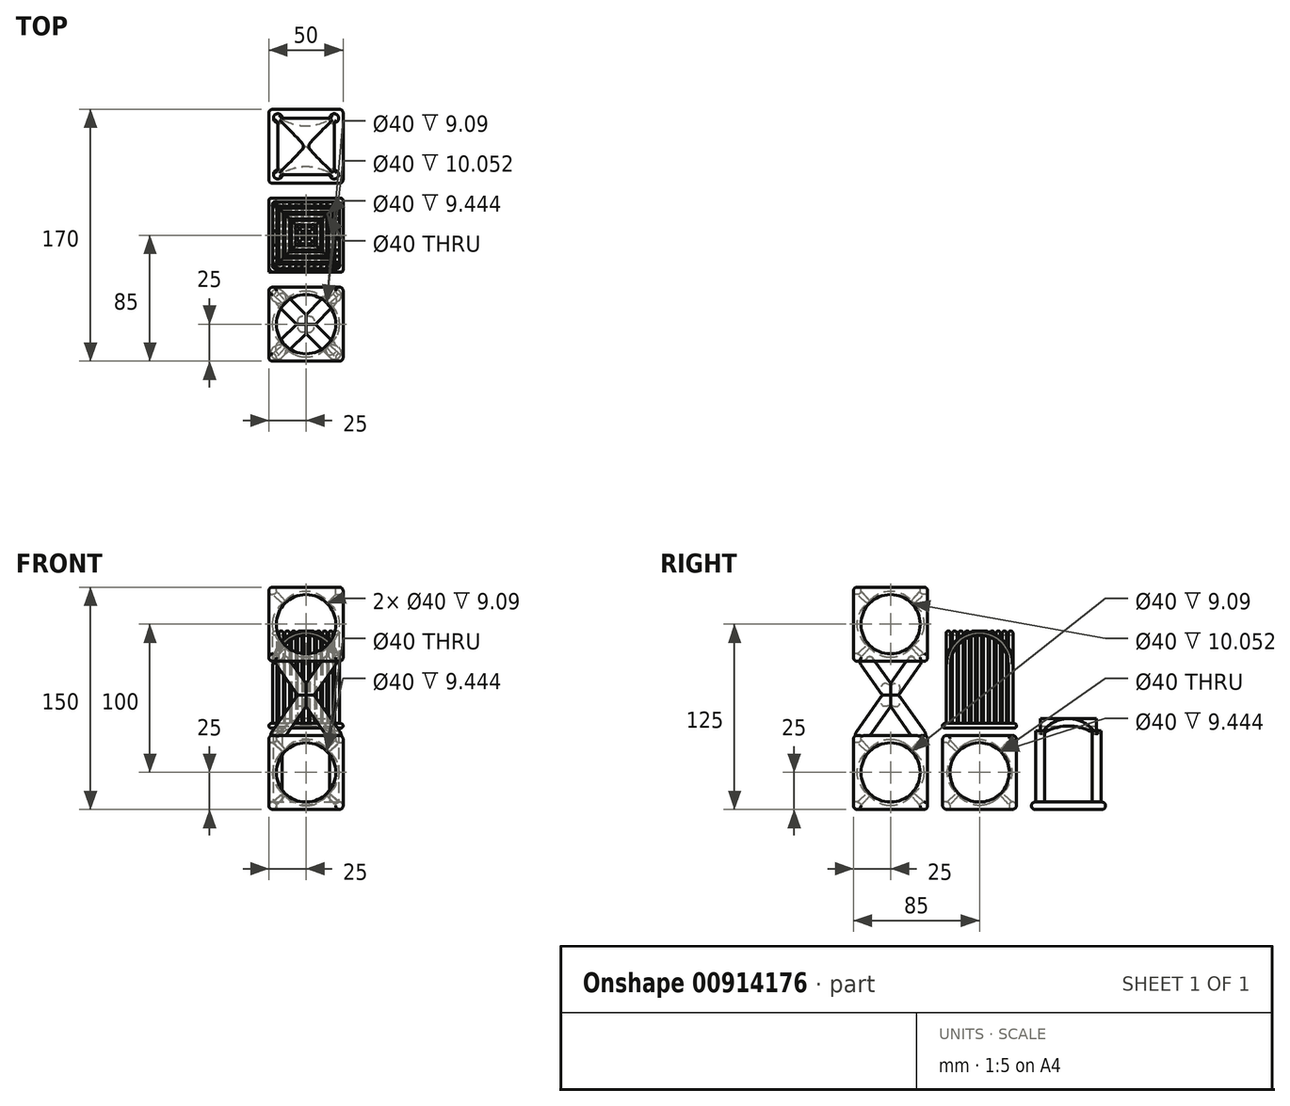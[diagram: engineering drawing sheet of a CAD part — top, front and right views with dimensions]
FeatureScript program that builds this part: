
annotation { "Feature Type Name" : "Feature", "Feature Type Description" : "" }
export const myFeature = defineFeature(function(context is Context, id is Id, definition is map)
    precondition{}
    {
        {
            var Q0;
            Q0=qCreatedBy(makeId("Front.planeOp"),FACE);
            var sketch = newSketch(context, id + "F0", { "sketchPlane" : qUnion([Q0])});
            skLineSegment(sketch, "E0.bottom", {"start": v(25, 25) * mm, "end": v(-25, 25) * mm});
            skLineSegment(sketch, "E0.top", {"start": v(25, -25) * mm, "end": v(-25, -25) * mm});
            skLineSegment(sketch, "E0.left", {"start": v(25, 25) * mm, "end": v(25, -25) * mm});
            skLineSegment(sketch, "E0.right", {"start": v(-25, 25) * mm, "end": v(-25, -25) * mm});
            skPoint(sketch, "E0.middle", {"position": v(0, 0) * mm});
            skSolve(sketch);
        }
        {
            var Q0;
            Q0=makeQuery(id+"F0.imprint","IMPRINT",FACE,{"disambiguationData":[TD([[makeQuery(id+"F0.imprint","IMPRINT",EDGE,{"derivedFrom":sQuery(id+"F0.wireOp",EDGE,"E0.bottom")}),1.0]])]});
            extrude(context, id + "F1", {"entities" : qUnion([Q0]), "endBound" : BoundingType.SYMMETRIC, "depth" : 50 * mm, "offsetDistance" : 25 * mm});
        }
        {
            var Q0;
            Q0=qCreatedBy(makeId("Front.planeOp"),FACE);
            var sketch = newSketch(context, id + "F2", { "sketchPlane" : qUnion([Q0])});
            skLineSegment(sketch, "E1", {"start": v(0, 99.5) * mm, "end": v(0, -126.75) * mm});
            skArc(sketch, "E2", {"start": v(0, -22.5) * mm, "mid": v(22.5, 0) * mm, "end": v(0, 22.5) * mm});
            skSolve(sketch);
        }
        {
            var Q0;
            Q0 = qSketchRegion(id + "F2", true);
            var Q1;
            Q1=sQuery(id+"F2.wireOp",EDGE,"E2");
            var Q2;
            Q2=sQuery(id+"F2.wireOp",EDGE,"E1");
            revolve(context, id + "F3", {"operationType" : NewBodyOperationType.REMOVE, "surfaceOperationType" : NewSurfaceOperationType.NEW, "entities" : qUnion([Q0]), "surfaceEntities" : qUnion([Q1]), "axis" : qUnion([Q2]), "revolveType" : RevolveType.FULL, "oppositeDirection" : true});
        }
        {
            var Q0;
            Q0=makeQuery(id+"F1.opExtrude","CAP_FACE",FACE,{"disambiguationData":[OSD([sQuery(id+"F0.wireOp",EDGE,"E0.bottom"),sQuery(id+"F0.wireOp",EDGE,"E0.top"),sQuery(id+"F0.wireOp",EDGE,"E0.left"),sQuery(id+"F0.wireOp",EDGE,"E0.right")])],"isStart":false});
            var sketch = newSketch(context, id + "F4", { "sketchPlane" : qUnion([Q0])});
            skCircle(sketch, "E3", {"center": v(0, 0) * mm, "radius": 20 * mm});
            skSolve(sketch);
        }
        {
            var Q0;
            Q0=makeQuery(id+"F1.opExtrude","SWEPT_FACE",FACE,{"disambiguationData":[OSD([sQuery(id+"F0.wireOp",EDGE,"E0.right")])]});
            var sketch = newSketch(context, id + "F5", { "sketchPlane" : qUnion([Q0])});
            skCircle(sketch, "E4", {"center": v(0, 0) * mm, "radius": 20 * mm});
            skSolve(sketch);
        }
        {
            var Q0;
            Q0=makeQuery(id+"F1.opExtrude","SWEPT_FACE",FACE,{"disambiguationData":[OSD([sQuery(id+"F0.wireOp",EDGE,"E0.top")])]});
            var sketch = newSketch(context, id + "F6", { "sketchPlane" : qUnion([Q0])});
            skCircle(sketch, "E5", {"center": v(0, 0) * mm, "radius": 20 * mm});
            skSolve(sketch);
        }
        {
            var Q0;
            Q0=makeQuery(id+"F4.imprint","IMPRINT",FACE,{"disambiguationData":[TD([[makeQuery(id+"F4.imprint","IMPRINT",EDGE,{"derivedFrom":sQuery(id+"F4.wireOp",EDGE,"E3")}),1.0]])]});
            extrude(context, id + "F7", {"entities" : qUnion([Q0]), "operationType" : NewBodyOperationType.REMOVE, "oppositeDirection" : true, "depth" : 51 * mm, "offsetDistance" : 25 * mm});
        }
        {
            var Q0;
            Q0=makeQuery(id+"F5.imprint","IMPRINT",FACE,{"disambiguationData":[TD([[makeQuery(id+"F5.imprint","IMPRINT",EDGE,{"derivedFrom":sQuery(id+"F5.wireOp",EDGE,"E4")}),1.0]])]});
            extrude(context, id + "F8", {"entities" : qUnion([Q0]), "operationType" : NewBodyOperationType.REMOVE, "oppositeDirection" : true, "depth" : 56.1 * mm, "offsetDistance" : 25 * mm});
        }
        {
            var Q0;
            Q0=makeQuery(id+"F6.imprint","IMPRINT",FACE,{"disambiguationData":[TD([[makeQuery(id+"F6.imprint","IMPRINT",EDGE,{"derivedFrom":sQuery(id+"F6.wireOp",EDGE,"E5")}),1.0]])]});
            extrude(context, id + "F9", {"entities" : qUnion([Q0]), "operationType" : NewBodyOperationType.REMOVE, "oppositeDirection" : true, "depth" : 54.1 * mm, "offsetDistance" : 25 * mm});
        }
        {
            var Q0;
            Q0=makeQuery(id+"F9.boolean.opBoolean","INTERSECT",EDGE,{"disambiguationData":[OD(1.0)],"derivedFrom":[makeQuery(id+"F7.boolean.opBoolean","COPY",FACE,{"disambiguationData":[TD([makeQuery(id+"F1.opExtrude","CAP_FACE",FACE,{"disambiguationData":[OSD([sQuery(id+"F0.wireOp",EDGE,"E0.bottom"),sQuery(id+"F0.wireOp",EDGE,"E0.top"),sQuery(id+"F0.wireOp",EDGE,"E0.left"),sQuery(id+"F0.wireOp",EDGE,"E0.right")])],"isStart":false})])],"derivedFrom":makeQuery(id+"F7.opExtrude","SWEPT_FACE",FACE,{"disambiguationData":[OSD([sQuery(id+"F4.wireOp",EDGE,"E3")])]})}),makeQuery(id+"F9.opExtrude","SWEPT_FACE",FACE,{"disambiguationData":[OSD([sQuery(id+"F6.wireOp",EDGE,"E5")])]})]});
            var Q1;
            {var subQ0=sQuery(id+"F0.wireOp",EDGE,"E0.right");Q1=makeQuery(id+"F9.boolean.opBoolean","INTERSECT",EDGE,{"disambiguationData":[OD(1.0)],"derivedFrom":[makeQuery(id+"F8.boolean.opBoolean","COPY",FACE,{"disambiguationData":[TD([makeQuery(id+"F1.opExtrude","SWEPT_FACE",FACE,{"disambiguationData":[OSD([subQ0])]})])],"derivedFrom":makeQuery(id+"F8.opExtrude","SWEPT_FACE",FACE,{"disambiguationData":[OSD([sQuery(id+"F5.wireOp",EDGE,"E4")])]})}),makeQuery(id+"F9.opExtrude","SWEPT_FACE",FACE,{"disambiguationData":[OSD([sQuery(id+"F6.wireOp",EDGE,"E5")])]})]});}
            var Q2;
            Q2=makeQuery(id+"F9.boolean.opBoolean","INTERSECT",EDGE,{"disambiguationData":[OD(1.0)],"derivedFrom":[makeQuery(id+"F7.boolean.opBoolean","COPY",FACE,{"disambiguationData":[TD([makeQuery(id+"F1.opExtrude","CAP_FACE",FACE,{"disambiguationData":[OSD([sQuery(id+"F0.wireOp",EDGE,"E0.bottom"),sQuery(id+"F0.wireOp",EDGE,"E0.top"),sQuery(id+"F0.wireOp",EDGE,"E0.left"),sQuery(id+"F0.wireOp",EDGE,"E0.right")])],"isStart":true})])],"derivedFrom":makeQuery(id+"F7.opExtrude","SWEPT_FACE",FACE,{"disambiguationData":[OSD([sQuery(id+"F4.wireOp",EDGE,"E3")])]})}),makeQuery(id+"F9.opExtrude","SWEPT_FACE",FACE,{"disambiguationData":[OSD([sQuery(id+"F6.wireOp",EDGE,"E5")])]})]});
            var Q3;
            {var subQ0=sQuery(id+"F0.wireOp",EDGE,"E0.left");Q3=makeQuery(id+"F9.boolean.opBoolean","INTERSECT",EDGE,{"disambiguationData":[OD(1.0)],"derivedFrom":[makeQuery(id+"F8.boolean.opBoolean","COPY",FACE,{"disambiguationData":[TD([makeQuery(id+"F1.opExtrude","SWEPT_FACE",FACE,{"disambiguationData":[OSD([subQ0])]})])],"derivedFrom":makeQuery(id+"F8.opExtrude","SWEPT_FACE",FACE,{"disambiguationData":[OSD([sQuery(id+"F5.wireOp",EDGE,"E4")])]})}),makeQuery(id+"F9.opExtrude","SWEPT_FACE",FACE,{"disambiguationData":[OSD([sQuery(id+"F6.wireOp",EDGE,"E5")])]})]});}
            var Q4;
            Q4=makeQuery(id+"F9.boolean.opBoolean","INTERSECT",EDGE,{"disambiguationData":[OD(0.0)],"derivedFrom":[makeQuery(id+"F7.boolean.opBoolean","COPY",FACE,{"disambiguationData":[TD([makeQuery(id+"F1.opExtrude","CAP_FACE",FACE,{"disambiguationData":[OSD([sQuery(id+"F0.wireOp",EDGE,"E0.bottom"),sQuery(id+"F0.wireOp",EDGE,"E0.top"),sQuery(id+"F0.wireOp",EDGE,"E0.left"),sQuery(id+"F0.wireOp",EDGE,"E0.right")])],"isStart":false})])],"derivedFrom":makeQuery(id+"F7.opExtrude","SWEPT_FACE",FACE,{"disambiguationData":[OSD([sQuery(id+"F4.wireOp",EDGE,"E3")])]})}),makeQuery(id+"F9.opExtrude","SWEPT_FACE",FACE,{"disambiguationData":[OSD([sQuery(id+"F6.wireOp",EDGE,"E5")])]})]});
            var Q5;
            Q5=makeQuery(id+"F9.boolean.opBoolean","INTERSECT",EDGE,{"disambiguationData":[OD(0.0)],"derivedFrom":[makeQuery(id+"F7.boolean.opBoolean","COPY",FACE,{"disambiguationData":[TD([makeQuery(id+"F1.opExtrude","CAP_FACE",FACE,{"disambiguationData":[OSD([sQuery(id+"F0.wireOp",EDGE,"E0.bottom"),sQuery(id+"F0.wireOp",EDGE,"E0.top"),sQuery(id+"F0.wireOp",EDGE,"E0.left"),sQuery(id+"F0.wireOp",EDGE,"E0.right")])],"isStart":true})])],"derivedFrom":makeQuery(id+"F7.opExtrude","SWEPT_FACE",FACE,{"disambiguationData":[OSD([sQuery(id+"F4.wireOp",EDGE,"E3")])]})}),makeQuery(id+"F9.opExtrude","SWEPT_FACE",FACE,{"disambiguationData":[OSD([sQuery(id+"F6.wireOp",EDGE,"E5")])]})]});
            var Q6;
            {var subQ0=sQuery(id+"F0.wireOp",EDGE,"E0.right");Q6=makeQuery(id+"F9.boolean.opBoolean","INTERSECT",EDGE,{"disambiguationData":[OD(0.0)],"derivedFrom":[makeQuery(id+"F8.boolean.opBoolean","COPY",FACE,{"disambiguationData":[TD([makeQuery(id+"F1.opExtrude","SWEPT_FACE",FACE,{"disambiguationData":[OSD([subQ0])]})])],"derivedFrom":makeQuery(id+"F8.opExtrude","SWEPT_FACE",FACE,{"disambiguationData":[OSD([sQuery(id+"F5.wireOp",EDGE,"E4")])]})}),makeQuery(id+"F9.opExtrude","SWEPT_FACE",FACE,{"disambiguationData":[OSD([sQuery(id+"F6.wireOp",EDGE,"E5")])]})]});}
            var Q7;
            {var subQ0=sQuery(id+"F0.wireOp",EDGE,"E0.left");Q7=makeQuery(id+"F9.boolean.opBoolean","INTERSECT",EDGE,{"disambiguationData":[OD(0.0)],"derivedFrom":[makeQuery(id+"F8.boolean.opBoolean","COPY",FACE,{"disambiguationData":[TD([makeQuery(id+"F1.opExtrude","SWEPT_FACE",FACE,{"disambiguationData":[OSD([subQ0])]})])],"derivedFrom":makeQuery(id+"F8.opExtrude","SWEPT_FACE",FACE,{"disambiguationData":[OSD([sQuery(id+"F5.wireOp",EDGE,"E4")])]})}),makeQuery(id+"F9.opExtrude","SWEPT_FACE",FACE,{"disambiguationData":[OSD([sQuery(id+"F6.wireOp",EDGE,"E5")])]})]});}
            var Q8;
            Q8=makeQuery(id+"F8.boolean.opBoolean","INTERSECT",EDGE,{"disambiguationData":[OD(1.0)],"derivedFrom":[makeQuery(id+"F7.boolean.opBoolean","COPY",FACE,{"disambiguationData":[TD([makeQuery(id+"F1.opExtrude","CAP_FACE",FACE,{"disambiguationData":[OSD([sQuery(id+"F0.wireOp",EDGE,"E0.bottom"),sQuery(id+"F0.wireOp",EDGE,"E0.top"),sQuery(id+"F0.wireOp",EDGE,"E0.left"),sQuery(id+"F0.wireOp",EDGE,"E0.right")])],"isStart":true})])],"derivedFrom":makeQuery(id+"F7.opExtrude","SWEPT_FACE",FACE,{"disambiguationData":[OSD([sQuery(id+"F4.wireOp",EDGE,"E3")])]})}),makeQuery(id+"F8.opExtrude","SWEPT_FACE",FACE,{"disambiguationData":[OSD([sQuery(id+"F5.wireOp",EDGE,"E4")])]})]});
            var Q9;
            Q9=makeQuery(id+"F8.boolean.opBoolean","INTERSECT",EDGE,{"disambiguationData":[OD(0.0)],"derivedFrom":[makeQuery(id+"F7.boolean.opBoolean","COPY",FACE,{"disambiguationData":[TD([makeQuery(id+"F1.opExtrude","CAP_FACE",FACE,{"disambiguationData":[OSD([sQuery(id+"F0.wireOp",EDGE,"E0.bottom"),sQuery(id+"F0.wireOp",EDGE,"E0.top"),sQuery(id+"F0.wireOp",EDGE,"E0.left"),sQuery(id+"F0.wireOp",EDGE,"E0.right")])],"isStart":true})])],"derivedFrom":makeQuery(id+"F7.opExtrude","SWEPT_FACE",FACE,{"disambiguationData":[OSD([sQuery(id+"F4.wireOp",EDGE,"E3")])]})}),makeQuery(id+"F8.opExtrude","SWEPT_FACE",FACE,{"disambiguationData":[OSD([sQuery(id+"F5.wireOp",EDGE,"E4")])]})]});
            var Q10;
            Q10=makeQuery(id+"F8.boolean.opBoolean","INTERSECT",EDGE,{"disambiguationData":[OD(0.0)],"derivedFrom":[makeQuery(id+"F7.boolean.opBoolean","COPY",FACE,{"disambiguationData":[TD([makeQuery(id+"F1.opExtrude","CAP_FACE",FACE,{"disambiguationData":[OSD([sQuery(id+"F0.wireOp",EDGE,"E0.bottom"),sQuery(id+"F0.wireOp",EDGE,"E0.top"),sQuery(id+"F0.wireOp",EDGE,"E0.left"),sQuery(id+"F0.wireOp",EDGE,"E0.right")])],"isStart":false})])],"derivedFrom":makeQuery(id+"F7.opExtrude","SWEPT_FACE",FACE,{"disambiguationData":[OSD([sQuery(id+"F4.wireOp",EDGE,"E3")])]})}),makeQuery(id+"F8.opExtrude","SWEPT_FACE",FACE,{"disambiguationData":[OSD([sQuery(id+"F5.wireOp",EDGE,"E4")])]})]});
            var Q11;
            Q11=makeQuery(id+"F8.boolean.opBoolean","INTERSECT",EDGE,{"disambiguationData":[OD(1.0)],"derivedFrom":[makeQuery(id+"F7.boolean.opBoolean","COPY",FACE,{"disambiguationData":[TD([makeQuery(id+"F1.opExtrude","CAP_FACE",FACE,{"disambiguationData":[OSD([sQuery(id+"F0.wireOp",EDGE,"E0.bottom"),sQuery(id+"F0.wireOp",EDGE,"E0.top"),sQuery(id+"F0.wireOp",EDGE,"E0.left"),sQuery(id+"F0.wireOp",EDGE,"E0.right")])],"isStart":false})])],"derivedFrom":makeQuery(id+"F7.opExtrude","SWEPT_FACE",FACE,{"disambiguationData":[OSD([sQuery(id+"F4.wireOp",EDGE,"E3")])]})}),makeQuery(id+"F8.opExtrude","SWEPT_FACE",FACE,{"disambiguationData":[OSD([sQuery(id+"F5.wireOp",EDGE,"E4")])]})]});
            var Q12;
            Q12=makeQuery(id+"F8.boolean.opBoolean","COPY",EDGE,{"derivedFrom":makeQuery(id+"F8.opExtrude","CAP_EDGE",EDGE,{"disambiguationData":[OSD([sQuery(id+"F5.wireOp",EDGE,"E4")])],"isStart":true})});
            var Q13;
            Q13=makeQuery(id+"F7.boolean.opBoolean","INTERSECT",EDGE,{"derivedFrom":[makeQuery(id+"F1.opExtrude","CAP_FACE",FACE,{"disambiguationData":[OSD([sQuery(id+"F0.wireOp",EDGE,"E0.bottom"),sQuery(id+"F0.wireOp",EDGE,"E0.top"),sQuery(id+"F0.wireOp",EDGE,"E0.left"),sQuery(id+"F0.wireOp",EDGE,"E0.right")])],"isStart":true}),makeQuery(id+"F7.opExtrude","SWEPT_FACE",FACE,{"disambiguationData":[OSD([sQuery(id+"F4.wireOp",EDGE,"E3")])]})]});
            var Q14;
            Q14=makeQuery(id+"F9.boolean.opBoolean","COPY",EDGE,{"derivedFrom":makeQuery(id+"F9.opExtrude","CAP_EDGE",EDGE,{"disambiguationData":[OSD([sQuery(id+"F6.wireOp",EDGE,"E5")])],"isStart":true})});
            var Q15;
            Q15=makeQuery(id+"F8.boolean.opBoolean","INTERSECT",EDGE,{"derivedFrom":[makeQuery(id+"F1.opExtrude","SWEPT_FACE",FACE,{"disambiguationData":[OSD([sQuery(id+"F0.wireOp",EDGE,"E0.left")])]}),makeQuery(id+"F8.opExtrude","SWEPT_FACE",FACE,{"disambiguationData":[OSD([sQuery(id+"F5.wireOp",EDGE,"E4")])]})]});
            var Q16;
            Q16=makeQuery(id+"F7.boolean.opBoolean","COPY",EDGE,{"derivedFrom":makeQuery(id+"F7.opExtrude","CAP_EDGE",EDGE,{"disambiguationData":[OSD([sQuery(id+"F4.wireOp",EDGE,"E3")])],"isStart":true})});
            var Q17;
            Q17=makeQuery(id+"F9.boolean.opBoolean","INTERSECT",EDGE,{"derivedFrom":[makeQuery(id+"F1.opExtrude","SWEPT_FACE",FACE,{"disambiguationData":[OSD([sQuery(id+"F0.wireOp",EDGE,"E0.bottom")])]}),makeQuery(id+"F9.opExtrude","SWEPT_FACE",FACE,{"disambiguationData":[OSD([sQuery(id+"F6.wireOp",EDGE,"E5")])]})]});
            fillet(context, id + "F10", {"entities" : qUnion([Q0, Q1, Q2, Q3, Q4, Q5, Q6, Q7, Q8, Q9, Q10, Q11, Q12, Q13, Q14, Q15, Q16, Q17]), "radius" : 2 * mm, "tangentPropagation" : true, "allowEdgeOverflow" : false});
        }
        {
            var Q0;
            Q0=makeQuery(id+"F1.opExtrude","SWEPT_EDGE",EDGE,{"disambiguationData":[OSD([sQuery(id+"F0.wireOp",EDGE,"E0.bottom"),sQuery(id+"F0.wireOp",EDGE,"E0.right")])]});
            var Q1;
            Q1=makeQuery(id+"F1.opExtrude","CAP_EDGE",EDGE,{"disambiguationData":[OSD([sQuery(id+"F0.wireOp",EDGE,"E0.bottom")])],"isStart":true});
            var Q2;
            Q2=makeQuery(id+"F1.opExtrude","SWEPT_EDGE",EDGE,{"disambiguationData":[OSD([sQuery(id+"F0.wireOp",EDGE,"E0.bottom"),sQuery(id+"F0.wireOp",EDGE,"E0.left")])]});
            var Q3;
            Q3=makeQuery(id+"F1.opExtrude","CAP_EDGE",EDGE,{"disambiguationData":[OSD([sQuery(id+"F0.wireOp",EDGE,"E0.bottom")])],"isStart":false});
            var Q4;
            Q4=makeQuery(id+"F1.opExtrude","SWEPT_EDGE",EDGE,{"disambiguationData":[OSD([sQuery(id+"F0.wireOp",EDGE,"E0.top"),sQuery(id+"F0.wireOp",EDGE,"E0.left")])]});
            var Q5;
            Q5=makeQuery(id+"F1.opExtrude","CAP_EDGE",EDGE,{"disambiguationData":[OSD([sQuery(id+"F0.wireOp",EDGE,"E0.top")])],"isStart":true});
            var Q6;
            Q6=makeQuery(id+"F1.opExtrude","CAP_EDGE",EDGE,{"disambiguationData":[OSD([sQuery(id+"F0.wireOp",EDGE,"E0.top")])],"isStart":false});
            var Q7;
            Q7=makeQuery(id+"F1.opExtrude","SWEPT_EDGE",EDGE,{"disambiguationData":[OSD([sQuery(id+"F0.wireOp",EDGE,"E0.top"),sQuery(id+"F0.wireOp",EDGE,"E0.right")])]});
            var Q8;
            Q8=makeQuery(id+"F1.opExtrude","CAP_EDGE",EDGE,{"disambiguationData":[OSD([sQuery(id+"F0.wireOp",EDGE,"E0.left")])],"isStart":true});
            var Q9;
            Q9=makeQuery(id+"F1.opExtrude","CAP_EDGE",EDGE,{"disambiguationData":[OSD([sQuery(id+"F0.wireOp",EDGE,"E0.left")])],"isStart":false});
            var Q10;
            Q10=makeQuery(id+"F1.opExtrude","CAP_EDGE",EDGE,{"disambiguationData":[OSD([sQuery(id+"F0.wireOp",EDGE,"E0.right")])],"isStart":true});
            var Q11;
            Q11=makeQuery(id+"F1.opExtrude","CAP_EDGE",EDGE,{"disambiguationData":[OSD([sQuery(id+"F0.wireOp",EDGE,"E0.right")])],"isStart":false});
            fillet(context, id + "F11", {"entities" : qUnion([Q0, Q1, Q2, Q3, Q4, Q5, Q6, Q7, Q8, Q9, Q10, Q11]), "radius" : 3 * mm, "tangentPropagation" : true, "allowEdgeOverflow" : false});
        }
        {
            var Q0;
            Q0=makeQuery(id+"F11.opFillet","SPLIT",FACE,{"disambiguationData":[OD(0.0)],"derivedFrom":makeQuery(id+"F1.opExtrude","SWEPT_FACE",FACE,{"disambiguationData":[OSD([sQuery(id+"F0.wireOp",EDGE,"E0.bottom")])]})});
            cPlane(context, id + "F12", {"entities" : qUnion([Q0]), "cplaneType" : CPlaneType.OFFSET, "offset" : 5 * mm, "width" : 150 * mm, "height" : 150 * mm});
        }
        {
            var Q0;
            Q0=qCreatedBy(id+"F12.planeOp",FACE);
            var sketch = newSketch(context, id + "F13", { "sketchPlane" : qUnion([Q0])});
            skLineSegment(sketch, "E6.bottom", {"start": v(-25, 25) * mm, "end": v(25, 25) * mm});
            skLineSegment(sketch, "E6.top", {"start": v(-25, -25) * mm, "end": v(25, -25) * mm});
            skLineSegment(sketch, "E6.left", {"start": v(-25, 25) * mm, "end": v(-25, -25) * mm});
            skLineSegment(sketch, "E6.right", {"start": v(25, 25) * mm, "end": v(25, -25) * mm});
            skPoint(sketch, "E6.middle", {"position": v(0, 0) * mm});
            skSolve(sketch);
        }
        {
            var Q0;
            Q0=makeQuery(id+"F13.imprint","IMPRINT",FACE,{"disambiguationData":[TD([[makeQuery(id+"F13.imprint","IMPRINT",EDGE,{"derivedFrom":sQuery(id+"F13.wireOp",EDGE,"E6.bottom")}),-1.0]])]});
            extrude(context, id + "F14", {"entities" : qUnion([Q0]), "depth" : 3 * mm, "offsetDistance" : 25 * mm});
        }
        {
            var Q0;
            Q0=makeQuery(id+"F14.opExtrude","CAP_EDGE",EDGE,{"disambiguationData":[OSD([sQuery(id+"F13.wireOp",EDGE,"E6.top")])],"isStart":false});
            var Q1;
            Q1=makeQuery(id+"F14.opExtrude","CAP_EDGE",EDGE,{"disambiguationData":[OSD([sQuery(id+"F13.wireOp",EDGE,"E6.right")])],"isStart":false});
            var Q2;
            Q2=makeQuery(id+"F14.opExtrude","CAP_EDGE",EDGE,{"disambiguationData":[OSD([sQuery(id+"F13.wireOp",EDGE,"E6.bottom")])],"isStart":false});
            var Q3;
            Q3=makeQuery(id+"F14.opExtrude","CAP_EDGE",EDGE,{"disambiguationData":[OSD([sQuery(id+"F13.wireOp",EDGE,"E6.left")])],"isStart":false});
            var Q4;
            Q4=makeQuery(id+"F14.opExtrude","CAP_EDGE",EDGE,{"disambiguationData":[OSD([sQuery(id+"F13.wireOp",EDGE,"E6.left")])],"isStart":true});
            var Q5;
            Q5=makeQuery(id+"F14.opExtrude","CAP_EDGE",EDGE,{"disambiguationData":[OSD([sQuery(id+"F13.wireOp",EDGE,"E6.top")])],"isStart":true});
            var Q6;
            Q6=makeQuery(id+"F14.opExtrude","CAP_EDGE",EDGE,{"disambiguationData":[OSD([sQuery(id+"F13.wireOp",EDGE,"E6.right")])],"isStart":true});
            var Q7;
            Q7=makeQuery(id+"F14.opExtrude","CAP_EDGE",EDGE,{"disambiguationData":[OSD([sQuery(id+"F13.wireOp",EDGE,"E6.bottom")])],"isStart":true});
            var Q8;
            Q8=makeQuery(id+"F14.opExtrude","SWEPT_EDGE",EDGE,{"disambiguationData":[OSD([sQuery(id+"F13.wireOp",EDGE,"E6.top"),sQuery(id+"F13.wireOp",EDGE,"E6.right")])]});
            var Q9;
            Q9=makeQuery(id+"F14.opExtrude","SWEPT_EDGE",EDGE,{"disambiguationData":[OSD([sQuery(id+"F13.wireOp",EDGE,"E6.bottom"),sQuery(id+"F13.wireOp",EDGE,"E6.right")])]});
            var Q10;
            Q10=makeQuery(id+"F14.opExtrude","SWEPT_EDGE",EDGE,{"disambiguationData":[OSD([sQuery(id+"F13.wireOp",EDGE,"E6.bottom"),sQuery(id+"F13.wireOp",EDGE,"E6.left")])]});
            fillet(context, id + "F15", {"entities" : qUnion([Q0, Q1, Q2, Q3, Q4, Q5, Q6, Q7, Q8, Q9, Q10]), "radius" : 1.5 * mm, "tangentPropagation" : true, "allowEdgeOverflow" : false});
        }
        {
            var Q0;
            Q0=makeQuery(id+"F14.opExtrude","CAP_FACE",FACE,{"disambiguationData":[OSD([sQuery(id+"F13.wireOp",EDGE,"E6.bottom"),sQuery(id+"F13.wireOp",EDGE,"E6.top"),sQuery(id+"F13.wireOp",EDGE,"E6.left"),sQuery(id+"F13.wireOp",EDGE,"E6.right")])],"isStart":false});
            var sketch = newSketch(context, id + "F16", { "sketchPlane" : qUnion([Q0])});
            skCircle(sketch, "E7", {"center": v(21, 21) * mm, "radius": 1.5 * mm});
            skCircle(sketch, "E8", {"center": v(21, 16.8) * mm, "radius": 1.5 * mm});
            skCircle(sketch, "E9", {"center": v(21, 12.6) * mm, "radius": 1.5 * mm});
            skCircle(sketch, "E10", {"center": v(21, 8.4) * mm, "radius": 1.5 * mm});
            skCircle(sketch, "E11", {"center": v(21, 4.2) * mm, "radius": 1.5 * mm});
            skCircle(sketch, "E12", {"center": v(21, 0) * mm, "radius": 1.5 * mm});
            skCircle(sketch, "E13", {"center": v(21, -4.2) * mm, "radius": 1.5 * mm});
            skCircle(sketch, "E14", {"center": v(21, -8.4) * mm, "radius": 1.5 * mm});
            skCircle(sketch, "E15", {"center": v(21, -12.6) * mm, "radius": 1.5 * mm});
            skCircle(sketch, "E16", {"center": v(21, -16.8) * mm, "radius": 1.5 * mm});
            skCircle(sketch, "E17", {"center": v(21, -21) * mm, "radius": 1.5 * mm});
            skCircle(sketch, "E18", {"center": v(16.8, -21) * mm, "radius": 1.5 * mm});
            skCircle(sketch, "E19", {"center": v(12.6, -21) * mm, "radius": 1.5 * mm});
            skCircle(sketch, "E20", {"center": v(8.4, -21) * mm, "radius": 1.5 * mm});
            skCircle(sketch, "E21", {"center": v(4.2, -21) * mm, "radius": 1.5 * mm});
            skCircle(sketch, "E22", {"center": v(0, -21) * mm, "radius": 1.5 * mm});
            skCircle(sketch, "E23", {"center": v(-4.2, -21) * mm, "radius": 1.5 * mm});
            skCircle(sketch, "E24", {"center": v(-8.4, -21) * mm, "radius": 1.5 * mm});
            skCircle(sketch, "E25", {"center": v(-12.6, -21) * mm, "radius": 1.5 * mm});
            skCircle(sketch, "E26", {"center": v(-16.8, -21) * mm, "radius": 1.5 * mm});
            skCircle(sketch, "E27", {"center": v(-21, -21) * mm, "radius": 1.5 * mm});
            skCircle(sketch, "E28", {"center": v(16.8, 21) * mm, "radius": 1.5 * mm});
            skCircle(sketch, "E29", {"center": v(12.6, 21) * mm, "radius": 1.5 * mm});
            skCircle(sketch, "E30", {"center": v(8.4, 21) * mm, "radius": 1.5 * mm});
            skCircle(sketch, "E31", {"center": v(4.2, 21) * mm, "radius": 1.5 * mm});
            skCircle(sketch, "E32", {"center": v(0, 21) * mm, "radius": 1.5 * mm});
            skCircle(sketch, "E33", {"center": v(-4.2, 21) * mm, "radius": 1.5 * mm});
            skCircle(sketch, "E34", {"center": v(-8.4, 21) * mm, "radius": 1.5 * mm});
            skCircle(sketch, "E35", {"center": v(-12.6, 21) * mm, "radius": 1.5 * mm});
            skCircle(sketch, "E36", {"center": v(-16.8, 21) * mm, "radius": 1.5 * mm});
            skCircle(sketch, "E37", {"center": v(-21, 21) * mm, "radius": 1.5 * mm});
            skCircle(sketch, "E38", {"center": v(-21, 16.8) * mm, "radius": 1.5 * mm});
            skCircle(sketch, "E39", {"center": v(-21, 12.6) * mm, "radius": 1.5 * mm});
            skCircle(sketch, "E40", {"center": v(-21, 8.4) * mm, "radius": 1.5 * mm});
            skCircle(sketch, "E41", {"center": v(-21, 4.2) * mm, "radius": 1.5 * mm});
            skCircle(sketch, "E42", {"center": v(-21, 0) * mm, "radius": 1.5 * mm});
            skCircle(sketch, "E43", {"center": v(-21, -4.2) * mm, "radius": 1.5 * mm});
            skCircle(sketch, "E44", {"center": v(-21, -8.4) * mm, "radius": 1.5 * mm});
            skCircle(sketch, "E45", {"center": v(-21, -12.6) * mm, "radius": 1.5 * mm});
            skCircle(sketch, "E46", {"center": v(-21, -16.8) * mm, "radius": 1.5 * mm});
            skSolve(sketch);
        }
        {
            var Q0;
            Q0 = qSketchRegion(id + "F16", true);
            extrude(context, id + "F17", {"entities" : qUnion([Q0]), "operationType" : NewBodyOperationType.ADD, "depth" : 40 * mm, "offsetDistance" : 25 * mm});
        }
        {
            var Q0;
            Q0=makeQuery(id+"F11.opFillet","SPLIT",FACE,{"disambiguationData":[OD(3.0)],"derivedFrom":makeQuery(id+"F1.opExtrude","CAP_FACE",FACE,{"disambiguationData":[OSD([sQuery(id+"F0.wireOp",EDGE,"E0.bottom"),sQuery(id+"F0.wireOp",EDGE,"E0.top"),sQuery(id+"F0.wireOp",EDGE,"E0.left"),sQuery(id+"F0.wireOp",EDGE,"E0.right")])],"isStart":false})});
            cPlane(context, id + "F18", {"entities" : qUnion([Q0]), "cplaneType" : CPlaneType.OFFSET, "offset" : 8.2 * mm, "oppositeDirection" : true, "width" : 150 * mm, "height" : 150 * mm});
        }
        {
            var Q0;
            Q0=qCreatedBy(id+"F18.planeOp",FACE);
            var sketch = newSketch(context, id + "F19", { "sketchPlane" : qUnion([Q0])});
            skArc(sketch, "E47", {"start": v(21, 73) * mm, "mid": v(0, 94) * mm, "end": v(-21, 73) * mm});
            skSolve(sketch);
        }
        {
            var Q0;
            Q0=qCreatedBy(id+"F18.planeOp",FACE);
            cPlane(context, id + "F20", {"entities" : qUnion([Q0]), "cplaneType" : CPlaneType.OFFSET, "offset" : 4.2 * mm, "oppositeDirection" : true, "width" : 150 * mm, "height" : 150 * mm});
        }
        {
            var Q0;
            Q0=qCreatedBy(id+"F20.planeOp",FACE);
            cPlane(context, id + "F21", {"entities" : qUnion([Q0]), "cplaneType" : CPlaneType.OFFSET, "offset" : 4.2 * mm, "oppositeDirection" : true, "width" : 150 * mm, "height" : 150 * mm});
        }
        {
            var Q0;
            Q0=qCreatedBy(id+"F21.planeOp",FACE);
            cPlane(context, id + "F22", {"entities" : qUnion([Q0]), "cplaneType" : CPlaneType.OFFSET, "offset" : 4.2 * mm, "oppositeDirection" : true, "width" : 150 * mm, "height" : 150 * mm});
        }
        {
            var Q0;
            Q0=qCreatedBy(makeId("Front.planeOp"),FACE);
            cPlane(context, id + "F23", {"entities" : qUnion([Q0]), "cplaneType" : CPlaneType.OFFSET, "offset" : 4.2 * mm, "oppositeDirection" : true, "width" : 150 * mm, "height" : 150 * mm});
        }
        {
            var Q0;
            Q0=qCreatedBy(id+"F23.planeOp",FACE);
            cPlane(context, id + "F24", {"entities" : qUnion([Q0]), "cplaneType" : CPlaneType.OFFSET, "offset" : 4.2 * mm, "oppositeDirection" : true, "width" : 150 * mm, "height" : 150 * mm});
        }
        {
            var Q0;
            Q0=qCreatedBy(id+"F24.planeOp",FACE);
            cPlane(context, id + "F25", {"entities" : qUnion([Q0]), "cplaneType" : CPlaneType.OFFSET, "offset" : 4.2 * mm, "oppositeDirection" : true, "width" : 150 * mm, "height" : 150 * mm});
        }
        {
            var Q0;
            Q0=qCreatedBy(id+"F25.planeOp",FACE);
            cPlane(context, id + "F26", {"entities" : qUnion([Q0]), "cplaneType" : CPlaneType.OFFSET, "offset" : 4.2 * mm, "oppositeDirection" : true, "width" : 150 * mm, "height" : 150 * mm});
        }
        {
            var Q0;
            Q0=qCreatedBy(id+"F20.planeOp",FACE);
            var sketch = newSketch(context, id + "F27", { "sketchPlane" : qUnion([Q0])});
            skArc(sketch, "E48", {"start": v(21, 73) * mm, "mid": v(0, 94) * mm, "end": v(-21, 73) * mm});
            skSolve(sketch);
        }
        {
            var Q0;
            Q0=qCreatedBy(id+"F21.planeOp",FACE);
            var sketch = newSketch(context, id + "F28", { "sketchPlane" : qUnion([Q0])});
            skArc(sketch, "E49", {"start": v(21, 73) * mm, "mid": v(0, 94) * mm, "end": v(-21, 73) * mm});
            skSolve(sketch);
        }
        {
            var Q0;
            Q0=qCreatedBy(id+"F22.planeOp",FACE);
            var sketch = newSketch(context, id + "F29", { "sketchPlane" : qUnion([Q0])});
            skArc(sketch, "E50", {"start": v(21, 73) * mm, "mid": v(0, 94) * mm, "end": v(-21, 73) * mm});
            skSolve(sketch);
        }
        {
            var Q0;
            Q0=qCreatedBy(makeId("Front.planeOp"),FACE);
            var sketch = newSketch(context, id + "F30", { "sketchPlane" : qUnion([Q0])});
            skArc(sketch, "E51", {"start": v(21, 73) * mm, "mid": v(0, 94) * mm, "end": v(-21, 73) * mm});
            skSolve(sketch);
        }
        {
            var Q0;
            Q0=qCreatedBy(id+"F23.planeOp",FACE);
            var sketch = newSketch(context, id + "F31", { "sketchPlane" : qUnion([Q0])});
            skArc(sketch, "E52", {"start": v(21, 73) * mm, "mid": v(0, 94) * mm, "end": v(-21, 73) * mm});
            skSolve(sketch);
        }
        {
            var Q0;
            Q0=qCreatedBy(id+"F24.planeOp",FACE);
            var sketch = newSketch(context, id + "F32", { "sketchPlane" : qUnion([Q0])});
            skArc(sketch, "E53", {"start": v(21, 73) * mm, "mid": v(0, 94) * mm, "end": v(-21, 73) * mm});
            skSolve(sketch);
        }
        {
            var Q0;
            Q0=qCreatedBy(id+"F25.planeOp",FACE);
            var sketch = newSketch(context, id + "F33", { "sketchPlane" : qUnion([Q0])});
            skArc(sketch, "E54", {"start": v(21, 73) * mm, "mid": v(0, 94) * mm, "end": v(-21, 73) * mm});
            skSolve(sketch);
        }
        {
            var Q0;
            Q0=qCreatedBy(id+"F26.planeOp",FACE);
            var sketch = newSketch(context, id + "F34", { "sketchPlane" : qUnion([Q0])});
            skArc(sketch, "E55", {"start": v(-21, 73) * mm, "mid": v(0, 94) * mm, "end": v(21, 73) * mm});
            skSolve(sketch);
        }
        {
            var Q0;
            Q0=makeQuery(id+"F17.opExtrude","CAP_FACE",FACE,{"disambiguationData":[OSD([sQuery(id+"F16.wireOp",EDGE,"E16")])],"isStart":false});
            var Q1;
            Q1=sQuery(id+"F19.wireOp",EDGE,"E47");
            sweep(context, id + "F35", {"operationType" : NewBodyOperationType.ADD, "profiles" : qUnion([Q0]), "path" : qUnion([Q1])});
        }
        {
            var Q0;
            Q0=makeQuery(id+"F17.opExtrude","CAP_FACE",FACE,{"disambiguationData":[OSD([sQuery(id+"F16.wireOp",EDGE,"E15")])],"isStart":false});
            var Q1;
            Q1=sQuery(id+"F27.wireOp",EDGE,"E48");
            sweep(context, id + "F36", {"operationType" : NewBodyOperationType.ADD, "profiles" : qUnion([Q0]), "path" : qUnion([Q1])});
        }
        {
            var Q0;
            Q0=makeQuery(id+"F17.opExtrude","CAP_FACE",FACE,{"disambiguationData":[OSD([sQuery(id+"F16.wireOp",EDGE,"E14")])],"isStart":false});
            var Q1;
            Q1=sQuery(id+"F28.wireOp",EDGE,"E49");
            sweep(context, id + "F37", {"operationType" : NewBodyOperationType.ADD, "profiles" : qUnion([Q0]), "path" : qUnion([Q1])});
        }
        {
            var Q0;
            Q0=makeQuery(id+"F17.opExtrude","CAP_FACE",FACE,{"disambiguationData":[OSD([sQuery(id+"F16.wireOp",EDGE,"E13")])],"isStart":false});
            var Q1;
            Q1=sQuery(id+"F29.wireOp",EDGE,"E50");
            sweep(context, id + "F38", {"operationType" : NewBodyOperationType.ADD, "profiles" : qUnion([Q0]), "path" : qUnion([Q1])});
        }
        {
            var Q0;
            Q0=makeQuery(id+"F17.opExtrude","CAP_FACE",FACE,{"disambiguationData":[OSD([sQuery(id+"F16.wireOp",EDGE,"E12")])],"isStart":false});
            var Q1;
            Q1=sQuery(id+"F30.wireOp",EDGE,"E51");
            sweep(context, id + "F39", {"operationType" : NewBodyOperationType.ADD, "profiles" : qUnion([Q0]), "path" : qUnion([Q1])});
        }
        {
            var Q0;
            Q0=makeQuery(id+"F17.opExtrude","CAP_FACE",FACE,{"disambiguationData":[OSD([sQuery(id+"F16.wireOp",EDGE,"E11")])],"isStart":false});
            var Q1;
            Q1=sQuery(id+"F31.wireOp",EDGE,"E52");
            sweep(context, id + "F40", {"operationType" : NewBodyOperationType.ADD, "profiles" : qUnion([Q0]), "path" : qUnion([Q1])});
        }
        {
            var Q0;
            Q0=makeQuery(id+"F17.opExtrude","CAP_FACE",FACE,{"disambiguationData":[OSD([sQuery(id+"F16.wireOp",EDGE,"E10")])],"isStart":false});
            var Q1;
            Q1=sQuery(id+"F32.wireOp",EDGE,"E53");
            sweep(context, id + "F41", {"operationType" : NewBodyOperationType.ADD, "profiles" : qUnion([Q0]), "path" : qUnion([Q1])});
        }
        {
            var Q0;
            Q0=makeQuery(id+"F17.opExtrude","CAP_FACE",FACE,{"disambiguationData":[OSD([sQuery(id+"F16.wireOp",EDGE,"E9")])],"isStart":false});
            var Q1;
            Q1=sQuery(id+"F33.wireOp",EDGE,"E54");
            sweep(context, id + "F42", {"operationType" : NewBodyOperationType.ADD, "profiles" : qUnion([Q0]), "path" : qUnion([Q1])});
        }
        {
            var Q0;
            Q0=makeQuery(id+"F17.opExtrude","CAP_FACE",FACE,{"disambiguationData":[OSD([sQuery(id+"F16.wireOp",EDGE,"E8")])],"isStart":false});
            var Q1;
            Q1=sQuery(id+"F34.wireOp",EDGE,"E55");
            sweep(context, id + "F43", {"operationType" : NewBodyOperationType.ADD, "profiles" : qUnion([Q0]), "path" : qUnion([Q1])});
        }
        {
            var Q0;
            Q0=qCreatedBy(makeId("Right.planeOp"),FACE);
            var sketch = newSketch(context, id + "F44", { "sketchPlane" : qUnion([Q0])});
            skArc(sketch, "E56", {"start": v(21, 73) * mm, "mid": v(0, 94) * mm, "end": v(-21, 73) * mm});
            skSolve(sketch);
        }
        {
            var Q0;
            Q0=qCreatedBy(makeId("Right.planeOp"),FACE);
            cPlane(context, id + "F45", {"entities" : qUnion([Q0]), "cplaneType" : CPlaneType.OFFSET, "offset" : 4.2 * mm, "width" : 150 * mm, "height" : 150 * mm});
        }
        {
            var Q0;
            Q0=qCreatedBy(id+"F45.planeOp",FACE);
            cPlane(context, id + "F46", {"entities" : qUnion([Q0]), "cplaneType" : CPlaneType.OFFSET, "offset" : 4.2 * mm, "width" : 150 * mm, "height" : 150 * mm});
        }
        {
            var Q0;
            Q0=qCreatedBy(id+"F46.planeOp",FACE);
            cPlane(context, id + "F47", {"entities" : qUnion([Q0]), "cplaneType" : CPlaneType.OFFSET, "offset" : 4.2 * mm, "width" : 150 * mm, "height" : 150 * mm});
        }
        {
            var Q0;
            Q0=qCreatedBy(makeId("Right.planeOp"),FACE);
            cPlane(context, id + "F48", {"entities" : qUnion([Q0]), "cplaneType" : CPlaneType.OFFSET, "offset" : 4.2 * mm, "oppositeDirection" : true, "width" : 150 * mm, "height" : 150 * mm});
        }
        {
            var Q0;
            Q0=qCreatedBy(id+"F48.planeOp",FACE);
            cPlane(context, id + "F49", {"entities" : qUnion([Q0]), "cplaneType" : CPlaneType.OFFSET, "offset" : 4.2 * mm, "oppositeDirection" : true, "width" : 150 * mm, "height" : 150 * mm});
        }
        {
            var Q0;
            Q0=qCreatedBy(id+"F49.planeOp",FACE);
            cPlane(context, id + "F50", {"entities" : qUnion([Q0]), "cplaneType" : CPlaneType.OFFSET, "offset" : 4.2 * mm, "oppositeDirection" : true, "width" : 150 * mm, "height" : 150 * mm});
        }
        {
            var Q0;
            Q0=qCreatedBy(id+"F50.planeOp",FACE);
            cPlane(context, id + "F51", {"entities" : qUnion([Q0]), "cplaneType" : CPlaneType.OFFSET, "offset" : 4.2 * mm, "oppositeDirection" : true, "width" : 150 * mm, "height" : 150 * mm});
        }
        {
            var Q0;
            Q0=qCreatedBy(id+"F45.planeOp",FACE);
            var sketch = newSketch(context, id + "F52", { "sketchPlane" : qUnion([Q0])});
            skArc(sketch, "E57", {"start": v(21, 73) * mm, "mid": v(0, 94) * mm, "end": v(-21, 73) * mm});
            skSolve(sketch);
        }
        {
            var Q0;
            Q0=makeQuery(id+"F11.opFillet","SPLIT",FACE,{"disambiguationData":[OD(2.0)],"derivedFrom":makeQuery(id+"F1.opExtrude","CAP_FACE",FACE,{"disambiguationData":[OSD([sQuery(id+"F0.wireOp",EDGE,"E0.bottom"),sQuery(id+"F0.wireOp",EDGE,"E0.top"),sQuery(id+"F0.wireOp",EDGE,"E0.left"),sQuery(id+"F0.wireOp",EDGE,"E0.right")])],"isStart":true})});
            cPlane(context, id + "F53", {"entities" : qUnion([Q0]), "cplaneType" : CPlaneType.OFFSET, "offset" : 0 * mm, "width" : 150 * mm, "height" : 150 * mm});
        }
        {
            var Q0;
            Q0=qCreatedBy(id+"F46.planeOp",FACE);
            var sketch = newSketch(context, id + "F54", { "sketchPlane" : qUnion([Q0])});
            skArc(sketch, "E58", {"start": v(21, 73) * mm, "mid": v(0, 94) * mm, "end": v(-21, 73) * mm});
            skSolve(sketch);
        }
        {
            var Q0;
            Q0=qCreatedBy(id+"F47.planeOp",FACE);
            var sketch = newSketch(context, id + "F55", { "sketchPlane" : qUnion([Q0])});
            skArc(sketch, "E59", {"start": v(21, 73) * mm, "mid": v(0, 94) * mm, "end": v(-21, 73) * mm});
            skSolve(sketch);
        }
        {
            var Q0;
            Q0=qCreatedBy(id+"F47.planeOp",FACE);
            cPlane(context, id + "F56", {"entities" : qUnion([Q0]), "cplaneType" : CPlaneType.OFFSET, "offset" : 4.2 * mm, "width" : 150 * mm, "height" : 150 * mm});
        }
        {
            var Q0;
            Q0=qCreatedBy(id+"F56.planeOp",FACE);
            var sketch = newSketch(context, id + "F57", { "sketchPlane" : qUnion([Q0])});
            skArc(sketch, "E60", {"start": v(21, 73) * mm, "mid": v(0, 94) * mm, "end": v(-21, 73) * mm});
            skSolve(sketch);
        }
        {
            var Q0;
            Q0=qCreatedBy(id+"F48.planeOp",FACE);
            var sketch = newSketch(context, id + "F58", { "sketchPlane" : qUnion([Q0])});
            skArc(sketch, "E61", {"start": v(-21, 73) * mm, "mid": v(0, 94) * mm, "end": v(21, 73) * mm});
            skSolve(sketch);
        }
        {
            var Q0;
            Q0=qCreatedBy(id+"F49.planeOp",FACE);
            var sketch = newSketch(context, id + "F59", { "sketchPlane" : qUnion([Q0])});
            skArc(sketch, "E62", {"start": v(-21, 73) * mm, "mid": v(0, 94) * mm, "end": v(21, 73) * mm});
            skSolve(sketch);
        }
        {
            var Q0;
            Q0=qCreatedBy(id+"F50.planeOp",FACE);
            var sketch = newSketch(context, id + "F60", { "sketchPlane" : qUnion([Q0])});
            skArc(sketch, "E63", {"start": v(-21, 73) * mm, "mid": v(0, 94) * mm, "end": v(21, 73) * mm});
            skSolve(sketch);
        }
        {
            var Q0;
            Q0=qCreatedBy(id+"F51.planeOp",FACE);
            var sketch = newSketch(context, id + "F61", { "sketchPlane" : qUnion([Q0])});
            skArc(sketch, "E64", {"start": v(-21, 73) * mm, "mid": v(0, 94) * mm, "end": v(21, 73) * mm});
            skSolve(sketch);
        }
        {
            var Q0;
            Q0=makeQuery(id+"F17.opExtrude","CAP_FACE",FACE,{"disambiguationData":[OSD([sQuery(id+"F16.wireOp",EDGE,"E26")])],"isStart":false});
            var Q1;
            Q1=sQuery(id+"F61.wireOp",EDGE,"E64");
            sweep(context, id + "F62", {"operationType" : NewBodyOperationType.ADD, "profiles" : qUnion([Q0]), "path" : qUnion([Q1])});
        }
        {
            var Q0;
            Q0=makeQuery(id+"F17.opExtrude","CAP_FACE",FACE,{"disambiguationData":[OSD([sQuery(id+"F16.wireOp",EDGE,"E25")])],"isStart":false});
            var Q1;
            Q1=sQuery(id+"F60.wireOp",EDGE,"E63");
            sweep(context, id + "F63", {"operationType" : NewBodyOperationType.ADD, "profiles" : qUnion([Q0]), "path" : qUnion([Q1])});
        }
        {
            var Q0;
            Q0=makeQuery(id+"F17.opExtrude","CAP_FACE",FACE,{"disambiguationData":[OSD([sQuery(id+"F16.wireOp",EDGE,"E24")])],"isStart":false});
            var Q1;
            Q1=sQuery(id+"F59.wireOp",EDGE,"E62");
            sweep(context, id + "F64", {"operationType" : NewBodyOperationType.ADD, "profiles" : qUnion([Q0]), "path" : qUnion([Q1])});
        }
        {
            var Q0;
            Q0=makeQuery(id+"F17.opExtrude","CAP_FACE",FACE,{"disambiguationData":[OSD([sQuery(id+"F16.wireOp",EDGE,"E23")])],"isStart":false});
            var Q1;
            Q1=sQuery(id+"F58.wireOp",EDGE,"E61");
            sweep(context, id + "F65", {"operationType" : NewBodyOperationType.ADD, "profiles" : qUnion([Q0]), "path" : qUnion([Q1])});
        }
        {
            var Q0;
            Q0=makeQuery(id+"F17.opExtrude","CAP_FACE",FACE,{"disambiguationData":[OSD([sQuery(id+"F16.wireOp",EDGE,"E22")])],"isStart":false});
            var Q1;
            Q1=sQuery(id+"F44.wireOp",EDGE,"E56");
            sweep(context, id + "F66", {"operationType" : NewBodyOperationType.ADD, "profiles" : qUnion([Q0]), "path" : qUnion([Q1])});
        }
        {
            var Q0;
            Q0=makeQuery(id+"F17.opExtrude","CAP_FACE",FACE,{"disambiguationData":[OSD([sQuery(id+"F16.wireOp",EDGE,"E21")])],"isStart":false});
            var Q1;
            Q1=sQuery(id+"F52.wireOp",EDGE,"E57");
            sweep(context, id + "F67", {"operationType" : NewBodyOperationType.ADD, "profiles" : qUnion([Q0]), "path" : qUnion([Q1])});
        }
        {
            var Q0;
            Q0=makeQuery(id+"F17.opExtrude","CAP_FACE",FACE,{"disambiguationData":[OSD([sQuery(id+"F16.wireOp",EDGE,"E20")])],"isStart":false});
            var Q1;
            Q1=sQuery(id+"F54.wireOp",EDGE,"E58");
            sweep(context, id + "F68", {"operationType" : NewBodyOperationType.ADD, "profiles" : qUnion([Q0]), "path" : qUnion([Q1])});
        }
        {
            var Q0;
            Q0=makeQuery(id+"F17.opExtrude","CAP_FACE",FACE,{"disambiguationData":[OSD([sQuery(id+"F16.wireOp",EDGE,"E19")])],"isStart":false});
            var Q1;
            Q1=sQuery(id+"F55.wireOp",EDGE,"E59");
            sweep(context, id + "F69", {"operationType" : NewBodyOperationType.ADD, "profiles" : qUnion([Q0]), "path" : qUnion([Q1])});
        }
        {
            var Q0;
            Q0=makeQuery(id+"F17.opExtrude","CAP_FACE",FACE,{"disambiguationData":[OSD([sQuery(id+"F16.wireOp",EDGE,"E18")])],"isStart":false});
            var Q1;
            Q1=sQuery(id+"F57.wireOp",EDGE,"E60");
            var Q2;
            Q2=sQuery(id+"F57.wireOp",EDGE,"E60");
            sweep(context, id + "F70", {"operationType" : NewBodyOperationType.ADD, "profiles" : qUnion([Q0]), "path" : qUnion([Q1, Q2])});
        }
        {
            var Q0;
            Q0=qCreatedBy(id+"F56.planeOp",FACE);
            cPlane(context, id + "F71", {"entities" : qUnion([Q0]), "cplaneType" : CPlaneType.OFFSET, "offset" : 4.2 * mm, "width" : 150 * mm, "height" : 150 * mm});
        }
        {
            var Q0;
            Q0=qCreatedBy(id+"F51.planeOp",FACE);
            cPlane(context, id + "F72", {"entities" : qUnion([Q0]), "cplaneType" : CPlaneType.OFFSET, "offset" : 4.2 * mm, "oppositeDirection" : true, "width" : 150 * mm, "height" : 150 * mm});
        }
        {
            var Q0;
            Q0=qCreatedBy(id+"F18.planeOp",FACE);
            cPlane(context, id + "F73", {"entities" : qUnion([Q0]), "cplaneType" : CPlaneType.OFFSET, "offset" : 4.2 * mm, "width" : 150 * mm, "height" : 150 * mm});
        }
        {
            var Q0;
            Q0=qCreatedBy(id+"F26.planeOp",FACE);
            cPlane(context, id + "F74", {"entities" : qUnion([Q0]), "cplaneType" : CPlaneType.OFFSET, "offset" : 4.2 * mm, "oppositeDirection" : true, "width" : 150 * mm, "height" : 150 * mm});
        }
        {
            var Q0;
            Q0=makeQuery(id+"F11.opFillet","SPLIT",FACE,{"disambiguationData":[OD(1.0)],"derivedFrom":makeQuery(id+"F1.opExtrude","SWEPT_FACE",FACE,{"disambiguationData":[OSD([sQuery(id+"F0.wireOp",EDGE,"E0.left")])]})});
            cPlane(context, id + "F75", {"entities" : qUnion([Q0]), "cplaneType" : CPlaneType.OFFSET, "offset" : 0 * mm, "width" : 150 * mm, "height" : 150 * mm});
        }
        {
            var Q0;
            Q0=qCreatedBy(id+"F73.planeOp",FACE);
            var sketch = newSketch(context, id + "F76", { "sketchPlane" : qUnion([Q0])});
            skArc(sketch, "E65", {"start": v(21, 73) * mm, "mid": v(0, 94) * mm, "end": v(-21, 73) * mm});
            skSolve(sketch);
        }
        {
            var Q0;
            Q0=qCreatedBy(id+"F74.planeOp",FACE);
            var sketch = newSketch(context, id + "F77", { "sketchPlane" : qUnion([Q0])});
            skArc(sketch, "E66", {"start": v(-21, 73) * mm, "mid": v(0, 94) * mm, "end": v(21, 73) * mm});
            skSolve(sketch);
        }
        {
            var Q0;
            Q0=qCreatedBy(id+"F71.planeOp",FACE);
            var sketch = newSketch(context, id + "F78", { "sketchPlane" : qUnion([Q0])});
            skArc(sketch, "E67", {"start": v(21, 73) * mm, "mid": v(0, 94) * mm, "end": v(-21, 73) * mm});
            skSolve(sketch);
        }
        {
            var Q0;
            Q0=qCreatedBy(id+"F72.planeOp",FACE);
            var sketch = newSketch(context, id + "F79", { "sketchPlane" : qUnion([Q0])});
            skArc(sketch, "E68", {"start": v(-21, 73) * mm, "mid": v(0, 94) * mm, "end": v(21, 73) * mm});
            skSolve(sketch);
        }
        {
            var Q0;
            Q0=makeQuery(id+"F17.opExtrude","CAP_FACE",FACE,{"disambiguationData":[OSD([sQuery(id+"F16.wireOp",EDGE,"E27")])],"isStart":false});
            var Q1;
            Q1=sQuery(id+"F79.wireOp",EDGE,"E68");
            sweep(context, id + "F80", {"operationType" : NewBodyOperationType.ADD, "profiles" : qUnion([Q0]), "path" : qUnion([Q1])});
        }
        {
            var Q0;
            Q0=makeQuery(id+"F17.opExtrude","CAP_FACE",FACE,{"disambiguationData":[OSD([sQuery(id+"F16.wireOp",EDGE,"E17")])],"isStart":false});
            var Q1;
            Q1=sQuery(id+"F76.wireOp",EDGE,"E65");
            sweep(context, id + "F81", {"operationType" : NewBodyOperationType.ADD, "profiles" : qUnion([Q0]), "path" : qUnion([Q1])});
        }
        {
            var Q0;
            Q0=makeQuery(id+"F17.opExtrude","CAP_FACE",FACE,{"disambiguationData":[OSD([sQuery(id+"F16.wireOp",EDGE,"E7")])],"isStart":false});
            var Q1;
            Q1=sQuery(id+"F78.wireOp",EDGE,"E67");
            sweep(context, id + "F82", {"operationType" : NewBodyOperationType.ADD, "profiles" : qUnion([Q0]), "path" : qUnion([Q1])});
        }
        {
            var Q0;
            Q0=makeQuery(id+"F14.opExtrude","CAP_FACE",FACE,{"disambiguationData":[OSD([sQuery(id+"F13.wireOp",EDGE,"E6.bottom"),sQuery(id+"F13.wireOp",EDGE,"E6.top"),sQuery(id+"F13.wireOp",EDGE,"E6.left"),sQuery(id+"F13.wireOp",EDGE,"E6.right")])],"isStart":false});
            cPlane(context, id + "F83", {"entities" : qUnion([Q0]), "cplaneType" : CPlaneType.OFFSET, "offset" : 40 * mm, "width" : 150 * mm, "height" : 150 * mm});
        }
        {
            var Q0;
            Q0=qCreatedBy(id+"F83.planeOp",FACE);
            var sketch = newSketch(context, id + "F84", { "sketchPlane" : qUnion([Q0])});
            skCircle(sketch, "E69", {"center": v(21, 21) * mm, "radius": 1.5 * mm});
            skSolve(sketch);
        }
        {
            var Q0;
            Q0 = qSketchRegion(id + "F84", true);
            var Q1;
            Q1=sQuery(id+"F77.wireOp",EDGE,"E66");
            sweep(context, id + "F85", {"operationType" : NewBodyOperationType.ADD, "profiles" : qUnion([Q0]), "path" : qUnion([Q1])});
        }
        {
            var Q0;
            Q0=makeQuery(id+"F11.opFillet","SPLIT",FACE,{"disambiguationData":[OD(2.0)],"derivedFrom":makeQuery(id+"F1.opExtrude","SWEPT_FACE",FACE,{"disambiguationData":[OSD([sQuery(id+"F0.wireOp",EDGE,"E0.top")])]})});
            cPlane(context, id + "F86", {"entities" : qUnion([Q0]), "cplaneType" : CPlaneType.OFFSET, "offset" : 0 * mm, "oppositeDirection" : true, "width" : 150 * mm, "height" : 150 * mm});
        }
        {
            var Q0;
            Q0=qCreatedBy(id+"F86.planeOp",FACE);
            var sketch = newSketch(context, id + "F87", { "sketchPlane" : qUnion([Q0])});
            skPoint(sketch, "E70", {"position": v(0, -60) * mm});
            skLineSegment(sketch, "E71.bottom", {"start": v(-22.5, -85) * mm, "end": v(22.5, -85) * mm});
            skLineSegment(sketch, "E71.top", {"start": v(-22.5, -35) * mm, "end": v(22.5, -35) * mm});
            skLineSegment(sketch, "E71.left", {"start": v(-25, -82.5) * mm, "end": v(-25, -37.5) * mm});
            skLineSegment(sketch, "E71.right", {"start": v(25, -82.5) * mm, "end": v(25, -37.5) * mm});
            skPoint(sketch, "E72.visualSharp", {"position": v(-25, -35) * mm});
            skArc(sketch, "E72.filletArc", {"start": v(-22.5, -35) * mm, "mid": v(-24.27, -35.73) * mm, "end": v(-25, -37.5) * mm});
            skPoint(sketch, "E73.visualSharp", {"position": v(-25, -85) * mm});
            skArc(sketch, "E73.filletArc", {"start": v(-25, -82.5) * mm, "mid": v(-24.27, -84.27) * mm, "end": v(-22.5, -85) * mm});
            skPoint(sketch, "E74.visualSharp", {"position": v(25, -85) * mm});
            skArc(sketch, "E74.filletArc", {"start": v(22.5, -85) * mm, "mid": v(24.27, -84.27) * mm, "end": v(25, -82.5) * mm});
            skPoint(sketch, "E75.visualSharp", {"position": v(25, -35) * mm});
            skArc(sketch, "E75.filletArc", {"start": v(25, -37.5) * mm, "mid": v(24.27, -35.73) * mm, "end": v(22.5, -35) * mm});
            skSolve(sketch);
        }
        {
            var Q0;
            Q0=makeQuery(id+"F87.imprint","IMPRINT",FACE,{"disambiguationData":[TD([[makeQuery(id+"F87.imprint","IMPRINT",EDGE,{"derivedFrom":sQuery(id+"F87.wireOp",EDGE,"E71.bottom")}),1.0]])]});
            extrude(context, id + "F88", {"entities" : qUnion([Q0]), "oppositeDirection" : true, "depth" : 5 * mm, "offsetDistance" : 25 * mm});
        }
        {
            var Q0;
            Q0=makeQuery(id+"F88.opExtrude","CAP_EDGE",EDGE,{"disambiguationData":[OSD([sQuery(id+"F87.wireOp",EDGE,"E71.right")])],"isStart":false});
            var Q1;
            Q1=makeQuery(id+"F88.opExtrude","CAP_EDGE",EDGE,{"disambiguationData":[OSD([sQuery(id+"F87.wireOp",EDGE,"E71.bottom")])],"isStart":false});
            var Q2;
            Q2=makeQuery(id+"F88.opExtrude","CAP_EDGE",EDGE,{"disambiguationData":[OSD([sQuery(id+"F87.wireOp",EDGE,"E71.top")])],"isStart":false});
            var Q3;
            Q3=makeQuery(id+"F88.opExtrude","CAP_EDGE",EDGE,{"disambiguationData":[OSD([sQuery(id+"F87.wireOp",EDGE,"E71.left")])],"isStart":false});
            var Q4;
            Q4=makeQuery(id+"F88.opExtrude","CAP_EDGE",EDGE,{"disambiguationData":[OSD([sQuery(id+"F87.wireOp",EDGE,"E71.right")])],"isStart":true});
            var Q5;
            Q5=makeQuery(id+"F88.opExtrude","CAP_EDGE",EDGE,{"disambiguationData":[OSD([sQuery(id+"F87.wireOp",EDGE,"E71.bottom")])],"isStart":true});
            var Q6;
            Q6=makeQuery(id+"F88.opExtrude","CAP_EDGE",EDGE,{"disambiguationData":[OSD([sQuery(id+"F87.wireOp",EDGE,"E71.top")])],"isStart":true});
            var Q7;
            Q7=makeQuery(id+"F88.opExtrude","CAP_EDGE",EDGE,{"disambiguationData":[OSD([sQuery(id+"F87.wireOp",EDGE,"E71.left")])],"isStart":true});
            fillet(context, id + "F89", {"entities" : qUnion([Q0, Q1, Q2, Q3, Q4, Q5, Q6, Q7]), "radius" : 2.5 * mm, "tangentPropagation" : true, "allowEdgeOverflow" : false});
        }
        {
            var Q0;
            Q0=makeQuery(id+"F88.opExtrude","CAP_FACE",FACE,{"disambiguationData":[OSD([sQuery(id+"F87.wireOp",EDGE,"E71.bottom"),sQuery(id+"F87.wireOp",EDGE,"E71.top"),sQuery(id+"F87.wireOp",EDGE,"E71.left"),sQuery(id+"F87.wireOp",EDGE,"E71.right"),sQuery(id+"F87.wireOp",EDGE,"E72.filletArc"),sQuery(id+"F87.wireOp",EDGE,"E73.filletArc"),sQuery(id+"F87.wireOp",EDGE,"E74.filletArc"),sQuery(id+"F87.wireOp",EDGE,"E75.filletArc")])],"isStart":false});
            var sketch = newSketch(context, id + "F90", { "sketchPlane" : qUnion([Q0])});
            skPoint(sketch, "E76", {"position": v(0, 60) * mm});
            skCircle(sketch, "E77", {"center": v(-19, 41) * mm, "radius": 3 * mm});
            skCircle(sketch, "E78", {"center": v(-19, 79) * mm, "radius": 3 * mm});
            skCircle(sketch, "E79", {"center": v(19, 79) * mm, "radius": 3 * mm});
            skCircle(sketch, "E80", {"center": v(19, 41) * mm, "radius": 3 * mm});
            skSolve(sketch);
        }
        {
            var Q0;
            Q0=makeQuery(id+"F90.imprint","IMPRINT",FACE,{"disambiguationData":[TD([[makeQuery(id+"F90.imprint","IMPRINT",EDGE,{"derivedFrom":sQuery(id+"F90.wireOp",EDGE,"E77")}),1.0]])]});
            var Q1;
            Q1=makeQuery(id+"F90.imprint","IMPRINT",FACE,{"disambiguationData":[TD([[makeQuery(id+"F90.imprint","IMPRINT",EDGE,{"derivedFrom":sQuery(id+"F90.wireOp",EDGE,"E78")}),1.0]])]});
            var Q2;
            Q2=makeQuery(id+"F90.imprint","IMPRINT",FACE,{"disambiguationData":[TD([[makeQuery(id+"F90.imprint","IMPRINT",EDGE,{"derivedFrom":sQuery(id+"F90.wireOp",EDGE,"E79")}),1.0]])]});
            var Q3;
            Q3=makeQuery(id+"F90.imprint","IMPRINT",FACE,{"disambiguationData":[TD([[makeQuery(id+"F90.imprint","IMPRINT",EDGE,{"derivedFrom":sQuery(id+"F90.wireOp",EDGE,"E80")}),1.0]])]});
            extrude(context, id + "F91", {"entities" : qUnion([Q0, Q1, Q2, Q3]), "operationType" : NewBodyOperationType.ADD, "depth" : 45 * mm, "offsetDistance" : 25 * mm});
        }
        {
            var Q0;
            Q0=makeQuery(id+"F11.opFillet","SPLIT",FACE,{"disambiguationData":[OD(1.0)],"derivedFrom":makeQuery(id+"F1.opExtrude","SWEPT_FACE",FACE,{"disambiguationData":[OSD([sQuery(id+"F0.wireOp",EDGE,"E0.left")])]})});
            cPlane(context, id + "F92", {"entities" : qUnion([Q0]), "cplaneType" : CPlaneType.OFFSET, "offset" : 6 * mm, "oppositeDirection" : true, "width" : 150 * mm, "height" : 150 * mm});
        }
        {
            var Q0;
            Q0=makeQuery(id+"F11.opFillet","SPLIT",FACE,{"disambiguationData":[OD(1.0)],"derivedFrom":makeQuery(id+"F1.opExtrude","CAP_FACE",FACE,{"disambiguationData":[OSD([sQuery(id+"F0.wireOp",EDGE,"E0.bottom"),sQuery(id+"F0.wireOp",EDGE,"E0.top"),sQuery(id+"F0.wireOp",EDGE,"E0.left"),sQuery(id+"F0.wireOp",EDGE,"E0.right")])],"isStart":true})});
            cPlane(context, id + "F93", {"entities" : qUnion([Q0]), "cplaneType" : CPlaneType.OFFSET, "offset" : 16 * mm, "width" : 150 * mm, "height" : 150 * mm});
        }
        {
            var Q0;
            Q0=qCreatedBy(id+"F92.planeOp",FACE);
            var sketch = newSketch(context, id + "F94", { "sketchPlane" : qUnion([Q0])});
            skPoint(sketch, "E81", {"position": v(60, -0.33) * mm});
            skPoint(sketch, "E82", {"position": v(79, 25) * mm});
            skPoint(sketch, "E83", {"position": v(41, 25) * mm});
            skArc(sketch, "E84", {"start": v(79, 25) * mm, "mid": v(60, 31.33) * mm, "end": v(41, 25) * mm});
            skPoint(sketch, "E85", {"position": v(60, 36.33) * mm});
            skPoint(sketch, "E85.positionSnap0", {"position": v(60, 31.33) * mm});
            skArc(sketch, "E86", {"start": v(79, 25) * mm, "mid": v(60, 36.33) * mm, "end": v(41, 25) * mm});
            skSolve(sketch);
        }
        {
            var Q0;
            Q0 = qSketchRegion(id + "F94", true);
            extrude(context, id + "F95", {"entities" : qUnion([Q0]), "oppositeDirection" : true, "depth" : 38 * mm, "offsetDistance" : 25 * mm});
        }
        {
            var Q0;
            Q0=qCreatedBy(id+"F93.planeOp",FACE);
            cPlane(context, id + "F96", {"entities" : qUnion([Q0]), "cplaneType" : CPlaneType.OFFSET, "offset" : 38 * mm, "width" : 150 * mm, "height" : 150 * mm});
        }
        {
            var Q0;
            Q0=qCreatedBy(id+"F96.planeOp",FACE);
            var sketch = newSketch(context, id + "F97", { "sketchPlane" : qUnion([Q0])});
            skPoint(sketch, "E87", {"position": v(19, 25) * mm});
            skPoint(sketch, "E88", {"position": v(-19, 25) * mm});
            skPoint(sketch, "E89", {"position": v(0, -0.33) * mm});
            skArc(sketch, "E90", {"start": v(19, 25) * mm, "mid": v(0, 31.4) * mm, "end": v(-19, 25) * mm});
            skPoint(sketch, "E91", {"position": v(0.06, 36.4) * mm});
            skPoint(sketch, "E91.positionSnap0", {"position": v(0, 31.4) * mm});
            skArc(sketch, "E92", {"start": v(19, 25) * mm, "mid": v(0, 36.4) * mm, "end": v(-19, 25) * mm});
            skSolve(sketch);
        }
        {
            var Q0;
            Q0=makeQuery(id+"F97.imprint","IMPRINT",FACE,{"disambiguationData":[TD([[makeQuery(id+"F97.imprint","IMPRINT",EDGE,{"derivedFrom":sQuery(id+"F97.wireOp",EDGE,"E90")}),-1.0]])]});
            extrude(context, id + "F98", {"entities" : qUnion([Q0]), "operationType" : NewBodyOperationType.ADD, "oppositeDirection" : true, "depth" : 38 * mm, "offsetDistance" : 25 * mm});
        }
        {
            var Q0;
            Q0=makeQuery(id+"F95.opExtrude","CAP_FACE",FACE,{"disambiguationData":[OSD([sQuery(id+"F94.wireOp",EDGE,"E84"),sQuery(id+"F94.wireOp",EDGE,"E86")])],"isStart":true});
            var sketch = newSketch(context, id + "F99", { "sketchPlane" : qUnion([Q0])});
            skPoint(sketch, "E93", {"position": v(60, -0.33) * mm});
            skArc(sketch, "E94", {"start": v(79, 25) * mm, "mid": v(60, 31.33) * mm, "end": v(41, 25) * mm});
            skLineSegment(sketch, "E95", {"start": v(41, 25) * mm, "end": v(79, 25) * mm});
            skSolve(sketch);
        }
        {
            var Q0;
            Q0=makeQuery(id+"F98.opExtrude","CAP_FACE",FACE,{"disambiguationData":[OSD([sQuery(id+"F97.wireOp",EDGE,"E90"),sQuery(id+"F97.wireOp",EDGE,"E92")])],"isStart":true});
            var sketch = newSketch(context, id + "F100", { "sketchPlane" : qUnion([Q0])});
            skPoint(sketch, "E96", {"position": v(0, -0.33) * mm});
            skArc(sketch, "E97", {"start": v(19, 25) * mm, "mid": v(0, 31.33) * mm, "end": v(-19, 25) * mm});
            skLineSegment(sketch, "E98", {"start": v(-19, 25) * mm, "end": v(19, 25) * mm});
            skSolve(sketch);
        }
        {
            var Q0;
            Q0=makeQuery(id+"F99.imprint","IMPRINT",FACE,{"disambiguationData":[TD([[makeQuery(id+"F99.imprint","IMPRINT",EDGE,{"derivedFrom":sQuery(id+"F99.wireOp",EDGE,"E94")}),1.0]])]});
            extrude(context, id + "F101", {"entities" : qUnion([Q0]), "operationType" : NewBodyOperationType.REMOVE, "oppositeDirection" : true, "depth" : 40 * mm, "offsetDistance" : 25 * mm});
        }
        {
            var Q0;
            Q0=makeQuery(id+"F100.imprint","IMPRINT",FACE,{"disambiguationData":[TD([[makeQuery(id+"F100.imprint","IMPRINT",EDGE,{"derivedFrom":sQuery(id+"F100.wireOp",EDGE,"E97")}),1.0]])]});
            extrude(context, id + "F102", {"entities" : qUnion([Q0]), "operationType" : NewBodyOperationType.REMOVE, "oppositeDirection" : true, "depth" : 40 * mm, "offsetDistance" : 25 * mm});
        }
        {
            var Q0;
            Q0=makeQuery(id+"F91.opExtrude","CAP_FACE",FACE,{"disambiguationData":[OSD([sQuery(id+"F90.wireOp",EDGE,"E80")])],"isStart":false});
            var sketch = newSketch(context, id + "F103", { "sketchPlane" : qUnion([Q0])});
            skCircle(sketch, "E99", {"center": v(19, 41) * mm, "radius": 3 * mm});
            skCircle(sketch, "E100", {"center": v(19, 79) * mm, "radius": 3 * mm});
            skCircle(sketch, "E101", {"center": v(-19, 79) * mm, "radius": 3 * mm});
            skCircle(sketch, "E102", {"center": v(-19, 41) * mm, "radius": 3 * mm});
            skSolve(sketch);
        }
        {
            var Q0;
            Q0 = qSketchRegion(id + "F103", true);
            extrude(context, id + "F104", {"entities" : qUnion([Q0]), "operationType" : NewBodyOperationType.ADD, "depth" : 3 * mm, "offsetDistance" : 25 * mm});
        }
        {
            var Q0;
            {var subQ0=sQuery(id+"F94.wireOp",EDGE,"E86");var subQ1=sQuery(id+"F94.wireOp",EDGE,"E84");var subQ2=sQuery(id+"F97.wireOp",EDGE,"E90");var subQ3=sQuery(id+"F97.wireOp",EDGE,"E92");var subQ4=makeQuery(id+"F98.opExtrude","SWEPT_FACE",FACE,{"disambiguationData":[OSD([subQ3])]});Q0=makeQuery(id+"F104.boolean.opBoolean","INTERSECT",EDGE,{"derivedFrom":[makeQuery(id+"F98.boolean.opBoolean","SPLIT",FACE,{"disambiguationData":[TD([makeQuery(id+"F95.opExtrude","SWEPT_FACE",FACE,{"disambiguationData":[OSD([subQ1])]}),makeQuery(id+"F95.opExtrude","CAP_FACE",FACE,{"disambiguationData":[OSD([subQ1,subQ0])],"isStart":true}),makeQuery(id+"F95.opExtrude","CAP_FACE",FACE,{"disambiguationData":[OSD([subQ1,subQ0])],"isStart":false}),makeQuery(id+"F95.opExtrude","SWEPT_FACE",FACE,{"disambiguationData":[OSD([subQ0])]}),makeQuery(id+"F98.opExtrude","SWEPT_FACE",FACE,{"disambiguationData":[OSD([subQ2])]}),makeQuery(id+"F98.opExtrude","CAP_FACE",FACE,{"disambiguationData":[OSD([subQ2,subQ3])],"isStart":true}),makeQuery(id+"F98.opExtrude","CAP_FACE",FACE,{"disambiguationData":[OSD([subQ2,subQ3])],"isStart":false}),subQ4])],"derivedFrom":subQ4}),makeQuery(id+"F104.opExtrude","CAP_FACE",FACE,{"disambiguationData":[OSD([sQuery(id+"F103.wireOp",EDGE,"E100")])],"isStart":false})]});}
            var Q1;
            {var subQ0=sQuery(id+"F97.wireOp",EDGE,"E90");var subQ1=sQuery(id+"F94.wireOp",EDGE,"E86");var subQ2=makeQuery(id+"F95.opExtrude","SWEPT_FACE",FACE,{"disambiguationData":[OSD([subQ1])]});var subQ3=sQuery(id+"F94.wireOp",EDGE,"E84");var subQ4=sQuery(id+"F97.wireOp",EDGE,"E92");Q1=makeQuery(id+"F104.boolean.opBoolean","INTERSECT",EDGE,{"derivedFrom":[makeQuery(id+"F98.boolean.opBoolean","SPLIT",FACE,{"disambiguationData":[TD([makeQuery(id+"F95.opExtrude","SWEPT_FACE",FACE,{"disambiguationData":[OSD([subQ3])]}),makeQuery(id+"F95.opExtrude","CAP_FACE",FACE,{"disambiguationData":[OSD([subQ3,subQ1])],"isStart":true}),subQ2,makeQuery(id+"F98.opExtrude","SWEPT_FACE",FACE,{"disambiguationData":[OSD([subQ0])]}),makeQuery(id+"F98.opExtrude","CAP_FACE",FACE,{"disambiguationData":[OSD([subQ0,subQ4])],"isStart":true}),makeQuery(id+"F98.opExtrude","CAP_FACE",FACE,{"disambiguationData":[OSD([subQ0,subQ4])],"isStart":false}),makeQuery(id+"F98.opExtrude","SWEPT_FACE",FACE,{"disambiguationData":[OSD([subQ4])]})])],"derivedFrom":subQ2}),makeQuery(id+"F104.opExtrude","CAP_FACE",FACE,{"disambiguationData":[OSD([sQuery(id+"F103.wireOp",EDGE,"E100")])],"isStart":false})]});}
            var Q2;
            Q2=makeQuery(id+"F104.boolean.opBoolean","INTERSECT",EDGE,{"derivedFrom":[makeQuery(id+"F95.opExtrude","CAP_FACE",FACE,{"disambiguationData":[OSD([sQuery(id+"F94.wireOp",EDGE,"E84"),sQuery(id+"F94.wireOp",EDGE,"E86")])],"isStart":true}),makeQuery(id+"F104.opExtrude","CAP_FACE",FACE,{"disambiguationData":[OSD([sQuery(id+"F103.wireOp",EDGE,"E100")])],"isStart":false})]});
            var Q3;
            Q3=makeQuery(id+"F104.boolean.opBoolean","INTERSECT",EDGE,{"derivedFrom":[makeQuery(id+"F95.opExtrude","CAP_FACE",FACE,{"disambiguationData":[OSD([sQuery(id+"F94.wireOp",EDGE,"E84"),sQuery(id+"F94.wireOp",EDGE,"E86")])],"isStart":true}),makeQuery(id+"F104.opExtrude","SWEPT_FACE",FACE,{"disambiguationData":[OSD([sQuery(id+"F103.wireOp",EDGE,"E100")])]})]});
            var Q4;
            {var subQ0=sQuery(id+"F97.wireOp",EDGE,"E90");var subQ1=makeQuery(id+"F98.opExtrude","SWEPT_FACE",FACE,{"disambiguationData":[OSD([subQ0])]});var subQ2=sQuery(id+"F94.wireOp",EDGE,"E86");var subQ3=makeQuery(id+"F95.opExtrude","SWEPT_FACE",FACE,{"disambiguationData":[OSD([subQ2])]});var subQ4=sQuery(id+"F94.wireOp",EDGE,"E84");var subQ5=makeQuery(id+"F95.opExtrude","CAP_FACE",FACE,{"disambiguationData":[OSD([subQ4,subQ2])],"isStart":true});var subQ6=makeQuery(id+"F95.opExtrude","SWEPT_FACE",FACE,{"disambiguationData":[OSD([subQ4])]});var subQ7=sQuery(id+"F97.wireOp",EDGE,"E92");var subQ8=makeQuery(id+"F98.opExtrude","CAP_FACE",FACE,{"disambiguationData":[OSD([subQ0,subQ7])],"isStart":true});var subQ9=makeQuery(id+"F98.opExtrude","CAP_FACE",FACE,{"disambiguationData":[OSD([subQ0,subQ7])],"isStart":false});var subQ10=makeQuery(id+"F98.opExtrude","SWEPT_FACE",FACE,{"disambiguationData":[OSD([subQ7])]});var subQ11=makeQuery(id+"F95.opExtrude","CAP_FACE",FACE,{"disambiguationData":[OSD([subQ4,subQ2])],"isStart":false});Q4=makeQuery(id+"F104.boolean.opBoolean","INTERSECT",EDGE,{"derivedFrom":[makeQuery(id+"F102.boolean.opBoolean","SPLIT",FACE,{"disambiguationData":[TD([subQ5])],"derivedFrom":makeQuery(id+"F101.boolean.opBoolean","MERGE",FACE,{"derivedFrom":[makeQuery(id+"F98.boolean.opBoolean","SPLIT",FACE,{"disambiguationData":[TD([subQ6,subQ5,subQ3,subQ1,subQ8,subQ9,subQ10])],"derivedFrom":subQ6}),makeQuery(id+"F98.boolean.opBoolean","SPLIT",FACE,{"disambiguationData":[TD([subQ6,subQ11,subQ3,subQ1,subQ8,subQ9,subQ10])],"derivedFrom":subQ6}),makeQuery(id+"F98.boolean.opBoolean","SPLIT",FACE,{"disambiguationData":[TD([subQ6,subQ5,subQ11,subQ3,subQ1,subQ8,subQ9,subQ10])],"derivedFrom":subQ6})],"fromTools":[makeQuery(id+"F101.opExtrude","SWEPT_FACE",FACE,{"disambiguationData":[OSD([sQuery(id+"F99.wireOp",EDGE,"E94")])]})]})}),makeQuery(id+"F104.opExtrude","SWEPT_FACE",FACE,{"disambiguationData":[OSD([sQuery(id+"F103.wireOp",EDGE,"E100")])]})]});}
            var Q5;
            {var subQ2=sQuery(id+"F97.wireOp",EDGE,"E90");var subQ3=sQuery(id+"F97.wireOp",EDGE,"E92");var subQ4=makeQuery(id+"F102.opExtrude","SWEPT_FACE",FACE,{"disambiguationData":[OSD([sQuery(id+"F100.wireOp",EDGE,"E97")])]});Q5=makeQuery(id+"F104.boolean.opBoolean","INTERSECT",EDGE,{"derivedFrom":[makeQuery(id+"F102.boolean.opBoolean","COPY",FACE,{"disambiguationData":[TD([makeQuery(id+"F98.opExtrude","CAP_FACE",FACE,{"disambiguationData":[OSD([subQ2,subQ3])],"isStart":true})])],"derivedFrom":subQ4}),makeQuery(id+"F104.opExtrude","SWEPT_FACE",FACE,{"disambiguationData":[OSD([sQuery(id+"F103.wireOp",EDGE,"E100")])]})]});}
            var Q6;
            Q6=makeQuery(id+"F104.boolean.opBoolean","INTERSECT",EDGE,{"derivedFrom":[makeQuery(id+"F98.opExtrude","CAP_FACE",FACE,{"disambiguationData":[OSD([sQuery(id+"F97.wireOp",EDGE,"E90"),sQuery(id+"F97.wireOp",EDGE,"E92")])],"isStart":true}),makeQuery(id+"F104.opExtrude","SWEPT_FACE",FACE,{"disambiguationData":[OSD([sQuery(id+"F103.wireOp",EDGE,"E100")])]})]});
            var Q7;
            Q7=makeQuery(id+"F104.boolean.opBoolean","INTERSECT",EDGE,{"derivedFrom":[makeQuery(id+"F98.opExtrude","CAP_FACE",FACE,{"disambiguationData":[OSD([sQuery(id+"F97.wireOp",EDGE,"E90"),sQuery(id+"F97.wireOp",EDGE,"E92")])],"isStart":true}),makeQuery(id+"F104.opExtrude","CAP_FACE",FACE,{"disambiguationData":[OSD([sQuery(id+"F103.wireOp",EDGE,"E100")])],"isStart":false})]});
            var Q8;
            Q8=makeQuery(id+"F104.boolean.opBoolean","INTERSECT",EDGE,{"derivedFrom":[makeQuery(id+"F98.opExtrude","CAP_FACE",FACE,{"disambiguationData":[OSD([sQuery(id+"F97.wireOp",EDGE,"E90"),sQuery(id+"F97.wireOp",EDGE,"E92")])],"isStart":false}),makeQuery(id+"F104.opExtrude","CAP_FACE",FACE,{"disambiguationData":[OSD([sQuery(id+"F103.wireOp",EDGE,"E99")])],"isStart":false})]});
            var Q9;
            {var subQ0=sQuery(id+"F94.wireOp",EDGE,"E86");var subQ1=sQuery(id+"F94.wireOp",EDGE,"E84");var subQ2=sQuery(id+"F97.wireOp",EDGE,"E90");var subQ3=sQuery(id+"F97.wireOp",EDGE,"E92");var subQ4=makeQuery(id+"F98.opExtrude","SWEPT_FACE",FACE,{"disambiguationData":[OSD([subQ3])]});Q9=makeQuery(id+"F104.boolean.opBoolean","INTERSECT",EDGE,{"derivedFrom":[makeQuery(id+"F98.boolean.opBoolean","SPLIT",FACE,{"disambiguationData":[TD([makeQuery(id+"F95.opExtrude","SWEPT_FACE",FACE,{"disambiguationData":[OSD([subQ1])]}),makeQuery(id+"F95.opExtrude","CAP_FACE",FACE,{"disambiguationData":[OSD([subQ1,subQ0])],"isStart":true}),makeQuery(id+"F95.opExtrude","CAP_FACE",FACE,{"disambiguationData":[OSD([subQ1,subQ0])],"isStart":false}),makeQuery(id+"F95.opExtrude","SWEPT_FACE",FACE,{"disambiguationData":[OSD([subQ0])]}),makeQuery(id+"F98.opExtrude","SWEPT_FACE",FACE,{"disambiguationData":[OSD([subQ2])]}),makeQuery(id+"F98.opExtrude","CAP_FACE",FACE,{"disambiguationData":[OSD([subQ2,subQ3])],"isStart":true}),makeQuery(id+"F98.opExtrude","CAP_FACE",FACE,{"disambiguationData":[OSD([subQ2,subQ3])],"isStart":false}),subQ4])],"derivedFrom":subQ4}),makeQuery(id+"F104.opExtrude","CAP_FACE",FACE,{"disambiguationData":[OSD([sQuery(id+"F103.wireOp",EDGE,"E99")])],"isStart":false})]});}
            var Q10;
            {var subQ0=sQuery(id+"F97.wireOp",EDGE,"E90");var subQ1=sQuery(id+"F94.wireOp",EDGE,"E86");var subQ2=makeQuery(id+"F95.opExtrude","SWEPT_FACE",FACE,{"disambiguationData":[OSD([subQ1])]});var subQ3=sQuery(id+"F94.wireOp",EDGE,"E84");var subQ4=sQuery(id+"F97.wireOp",EDGE,"E92");Q10=makeQuery(id+"F104.boolean.opBoolean","INTERSECT",EDGE,{"derivedFrom":[makeQuery(id+"F98.boolean.opBoolean","SPLIT",FACE,{"disambiguationData":[TD([makeQuery(id+"F95.opExtrude","SWEPT_FACE",FACE,{"disambiguationData":[OSD([subQ3])]}),makeQuery(id+"F95.opExtrude","CAP_FACE",FACE,{"disambiguationData":[OSD([subQ3,subQ1])],"isStart":true}),subQ2,makeQuery(id+"F98.opExtrude","SWEPT_FACE",FACE,{"disambiguationData":[OSD([subQ0])]}),makeQuery(id+"F98.opExtrude","CAP_FACE",FACE,{"disambiguationData":[OSD([subQ0,subQ4])],"isStart":true}),makeQuery(id+"F98.opExtrude","CAP_FACE",FACE,{"disambiguationData":[OSD([subQ0,subQ4])],"isStart":false}),makeQuery(id+"F98.opExtrude","SWEPT_FACE",FACE,{"disambiguationData":[OSD([subQ4])]})])],"derivedFrom":subQ2}),makeQuery(id+"F104.opExtrude","CAP_FACE",FACE,{"disambiguationData":[OSD([sQuery(id+"F103.wireOp",EDGE,"E99")])],"isStart":false})]});}
            var Q11;
            Q11=makeQuery(id+"F104.boolean.opBoolean","INTERSECT",EDGE,{"derivedFrom":[makeQuery(id+"F95.opExtrude","CAP_FACE",FACE,{"disambiguationData":[OSD([sQuery(id+"F94.wireOp",EDGE,"E84"),sQuery(id+"F94.wireOp",EDGE,"E86")])],"isStart":true}),makeQuery(id+"F104.opExtrude","CAP_FACE",FACE,{"disambiguationData":[OSD([sQuery(id+"F103.wireOp",EDGE,"E99")])],"isStart":false})]});
            var Q12;
            {var subQ0=sQuery(id+"F97.wireOp",EDGE,"E90");var subQ1=makeQuery(id+"F98.opExtrude","SWEPT_FACE",FACE,{"disambiguationData":[OSD([subQ0])]});var subQ2=sQuery(id+"F94.wireOp",EDGE,"E86");var subQ3=makeQuery(id+"F95.opExtrude","SWEPT_FACE",FACE,{"disambiguationData":[OSD([subQ2])]});var subQ4=sQuery(id+"F94.wireOp",EDGE,"E84");var subQ5=makeQuery(id+"F95.opExtrude","CAP_FACE",FACE,{"disambiguationData":[OSD([subQ4,subQ2])],"isStart":true});var subQ6=makeQuery(id+"F95.opExtrude","SWEPT_FACE",FACE,{"disambiguationData":[OSD([subQ4])]});var subQ7=sQuery(id+"F97.wireOp",EDGE,"E92");var subQ8=makeQuery(id+"F98.opExtrude","CAP_FACE",FACE,{"disambiguationData":[OSD([subQ0,subQ7])],"isStart":true});var subQ9=makeQuery(id+"F98.opExtrude","CAP_FACE",FACE,{"disambiguationData":[OSD([subQ0,subQ7])],"isStart":false});var subQ10=makeQuery(id+"F98.opExtrude","SWEPT_FACE",FACE,{"disambiguationData":[OSD([subQ7])]});var subQ11=makeQuery(id+"F95.opExtrude","CAP_FACE",FACE,{"disambiguationData":[OSD([subQ4,subQ2])],"isStart":false});Q12=makeQuery(id+"F104.boolean.opBoolean","INTERSECT",EDGE,{"derivedFrom":[makeQuery(id+"F102.boolean.opBoolean","SPLIT",FACE,{"disambiguationData":[TD([subQ5])],"derivedFrom":makeQuery(id+"F101.boolean.opBoolean","MERGE",FACE,{"derivedFrom":[makeQuery(id+"F98.boolean.opBoolean","SPLIT",FACE,{"disambiguationData":[TD([subQ6,subQ5,subQ3,subQ1,subQ8,subQ9,subQ10])],"derivedFrom":subQ6}),makeQuery(id+"F98.boolean.opBoolean","SPLIT",FACE,{"disambiguationData":[TD([subQ6,subQ11,subQ3,subQ1,subQ8,subQ9,subQ10])],"derivedFrom":subQ6}),makeQuery(id+"F98.boolean.opBoolean","SPLIT",FACE,{"disambiguationData":[TD([subQ6,subQ5,subQ11,subQ3,subQ1,subQ8,subQ9,subQ10])],"derivedFrom":subQ6})],"fromTools":[makeQuery(id+"F101.opExtrude","SWEPT_FACE",FACE,{"disambiguationData":[OSD([sQuery(id+"F99.wireOp",EDGE,"E94")])]})]})}),makeQuery(id+"F104.opExtrude","SWEPT_FACE",FACE,{"disambiguationData":[OSD([sQuery(id+"F103.wireOp",EDGE,"E99")])]})]});}
            var Q13;
            {var subQ2=sQuery(id+"F97.wireOp",EDGE,"E90");var subQ3=sQuery(id+"F97.wireOp",EDGE,"E92");var subQ4=makeQuery(id+"F102.opExtrude","SWEPT_FACE",FACE,{"disambiguationData":[OSD([sQuery(id+"F100.wireOp",EDGE,"E97")])]});Q13=makeQuery(id+"F104.boolean.opBoolean","INTERSECT",EDGE,{"derivedFrom":[makeQuery(id+"F102.boolean.opBoolean","COPY",FACE,{"disambiguationData":[TD([makeQuery(id+"F98.opExtrude","CAP_FACE",FACE,{"disambiguationData":[OSD([subQ2,subQ3])],"isStart":false})])],"derivedFrom":subQ4}),makeQuery(id+"F104.opExtrude","SWEPT_FACE",FACE,{"disambiguationData":[OSD([sQuery(id+"F103.wireOp",EDGE,"E99")])]})]});}
            var Q14;
            Q14=makeQuery(id+"F104.boolean.opBoolean","INTERSECT",EDGE,{"derivedFrom":[makeQuery(id+"F98.opExtrude","CAP_FACE",FACE,{"disambiguationData":[OSD([sQuery(id+"F97.wireOp",EDGE,"E90"),sQuery(id+"F97.wireOp",EDGE,"E92")])],"isStart":false}),makeQuery(id+"F104.opExtrude","SWEPT_FACE",FACE,{"disambiguationData":[OSD([sQuery(id+"F103.wireOp",EDGE,"E99")])]})]});
            var Q15;
            Q15=makeQuery(id+"F104.boolean.opBoolean","INTERSECT",EDGE,{"derivedFrom":[makeQuery(id+"F95.opExtrude","CAP_FACE",FACE,{"disambiguationData":[OSD([sQuery(id+"F94.wireOp",EDGE,"E84"),sQuery(id+"F94.wireOp",EDGE,"E86")])],"isStart":true}),makeQuery(id+"F104.opExtrude","SWEPT_FACE",FACE,{"disambiguationData":[OSD([sQuery(id+"F103.wireOp",EDGE,"E99")])]})]});
            var Q16;
            Q16=makeQuery(id+"F104.boolean.opBoolean","INTERSECT",EDGE,{"derivedFrom":[makeQuery(id+"F98.opExtrude","CAP_FACE",FACE,{"disambiguationData":[OSD([sQuery(id+"F97.wireOp",EDGE,"E90"),sQuery(id+"F97.wireOp",EDGE,"E92")])],"isStart":false}),makeQuery(id+"F104.opExtrude","CAP_FACE",FACE,{"disambiguationData":[OSD([sQuery(id+"F103.wireOp",EDGE,"E102")])],"isStart":false})]});
            var Q17;
            {var subQ0=sQuery(id+"F94.wireOp",EDGE,"E86");var subQ1=sQuery(id+"F94.wireOp",EDGE,"E84");var subQ2=sQuery(id+"F97.wireOp",EDGE,"E90");var subQ3=sQuery(id+"F97.wireOp",EDGE,"E92");var subQ4=makeQuery(id+"F98.opExtrude","SWEPT_FACE",FACE,{"disambiguationData":[OSD([subQ3])]});Q17=makeQuery(id+"F104.boolean.opBoolean","INTERSECT",EDGE,{"derivedFrom":[makeQuery(id+"F98.boolean.opBoolean","SPLIT",FACE,{"disambiguationData":[TD([makeQuery(id+"F95.opExtrude","SWEPT_FACE",FACE,{"disambiguationData":[OSD([subQ1])]}),makeQuery(id+"F95.opExtrude","CAP_FACE",FACE,{"disambiguationData":[OSD([subQ1,subQ0])],"isStart":true}),makeQuery(id+"F95.opExtrude","CAP_FACE",FACE,{"disambiguationData":[OSD([subQ1,subQ0])],"isStart":false}),makeQuery(id+"F95.opExtrude","SWEPT_FACE",FACE,{"disambiguationData":[OSD([subQ0])]}),makeQuery(id+"F98.opExtrude","SWEPT_FACE",FACE,{"disambiguationData":[OSD([subQ2])]}),makeQuery(id+"F98.opExtrude","CAP_FACE",FACE,{"disambiguationData":[OSD([subQ2,subQ3])],"isStart":true}),makeQuery(id+"F98.opExtrude","CAP_FACE",FACE,{"disambiguationData":[OSD([subQ2,subQ3])],"isStart":false}),subQ4])],"derivedFrom":subQ4}),makeQuery(id+"F104.opExtrude","CAP_FACE",FACE,{"disambiguationData":[OSD([sQuery(id+"F103.wireOp",EDGE,"E102")])],"isStart":false})]});}
            var Q18;
            {var subQ0=sQuery(id+"F97.wireOp",EDGE,"E90");var subQ1=sQuery(id+"F94.wireOp",EDGE,"E86");var subQ2=makeQuery(id+"F95.opExtrude","SWEPT_FACE",FACE,{"disambiguationData":[OSD([subQ1])]});var subQ3=sQuery(id+"F94.wireOp",EDGE,"E84");var subQ4=sQuery(id+"F97.wireOp",EDGE,"E92");Q18=makeQuery(id+"F104.boolean.opBoolean","INTERSECT",EDGE,{"derivedFrom":[makeQuery(id+"F98.boolean.opBoolean","SPLIT",FACE,{"disambiguationData":[TD([makeQuery(id+"F95.opExtrude","SWEPT_FACE",FACE,{"disambiguationData":[OSD([subQ3])]}),makeQuery(id+"F95.opExtrude","CAP_FACE",FACE,{"disambiguationData":[OSD([subQ3,subQ1])],"isStart":false}),subQ2,makeQuery(id+"F98.opExtrude","SWEPT_FACE",FACE,{"disambiguationData":[OSD([subQ0])]}),makeQuery(id+"F98.opExtrude","CAP_FACE",FACE,{"disambiguationData":[OSD([subQ0,subQ4])],"isStart":true}),makeQuery(id+"F98.opExtrude","CAP_FACE",FACE,{"disambiguationData":[OSD([subQ0,subQ4])],"isStart":false}),makeQuery(id+"F98.opExtrude","SWEPT_FACE",FACE,{"disambiguationData":[OSD([subQ4])]})])],"derivedFrom":subQ2}),makeQuery(id+"F104.opExtrude","CAP_FACE",FACE,{"disambiguationData":[OSD([sQuery(id+"F103.wireOp",EDGE,"E102")])],"isStart":false})]});}
            var Q19;
            Q19=makeQuery(id+"F104.boolean.opBoolean","INTERSECT",EDGE,{"derivedFrom":[makeQuery(id+"F95.opExtrude","CAP_FACE",FACE,{"disambiguationData":[OSD([sQuery(id+"F94.wireOp",EDGE,"E84"),sQuery(id+"F94.wireOp",EDGE,"E86")])],"isStart":false}),makeQuery(id+"F104.opExtrude","CAP_FACE",FACE,{"disambiguationData":[OSD([sQuery(id+"F103.wireOp",EDGE,"E102")])],"isStart":false})]});
            var Q20;
            Q20=makeQuery(id+"F104.boolean.opBoolean","INTERSECT",EDGE,{"derivedFrom":[makeQuery(id+"F95.opExtrude","CAP_FACE",FACE,{"disambiguationData":[OSD([sQuery(id+"F94.wireOp",EDGE,"E84"),sQuery(id+"F94.wireOp",EDGE,"E86")])],"isStart":false}),makeQuery(id+"F104.opExtrude","SWEPT_FACE",FACE,{"disambiguationData":[OSD([sQuery(id+"F103.wireOp",EDGE,"E102")])]})]});
            var Q21;
            {var subQ0=sQuery(id+"F97.wireOp",EDGE,"E90");var subQ1=makeQuery(id+"F98.opExtrude","SWEPT_FACE",FACE,{"disambiguationData":[OSD([subQ0])]});var subQ2=sQuery(id+"F94.wireOp",EDGE,"E86");var subQ3=makeQuery(id+"F95.opExtrude","SWEPT_FACE",FACE,{"disambiguationData":[OSD([subQ2])]});var subQ4=sQuery(id+"F94.wireOp",EDGE,"E84");var subQ5=makeQuery(id+"F95.opExtrude","CAP_FACE",FACE,{"disambiguationData":[OSD([subQ4,subQ2])],"isStart":false});var subQ6=makeQuery(id+"F95.opExtrude","SWEPT_FACE",FACE,{"disambiguationData":[OSD([subQ4])]});var subQ7=sQuery(id+"F97.wireOp",EDGE,"E92");var subQ8=makeQuery(id+"F98.opExtrude","CAP_FACE",FACE,{"disambiguationData":[OSD([subQ0,subQ7])],"isStart":true});var subQ9=makeQuery(id+"F98.opExtrude","CAP_FACE",FACE,{"disambiguationData":[OSD([subQ0,subQ7])],"isStart":false});var subQ10=makeQuery(id+"F98.opExtrude","SWEPT_FACE",FACE,{"disambiguationData":[OSD([subQ7])]});var subQ11=makeQuery(id+"F95.opExtrude","CAP_FACE",FACE,{"disambiguationData":[OSD([subQ4,subQ2])],"isStart":true});Q21=makeQuery(id+"F104.boolean.opBoolean","INTERSECT",EDGE,{"derivedFrom":[makeQuery(id+"F102.boolean.opBoolean","SPLIT",FACE,{"disambiguationData":[TD([subQ5])],"derivedFrom":makeQuery(id+"F101.boolean.opBoolean","MERGE",FACE,{"derivedFrom":[makeQuery(id+"F98.boolean.opBoolean","SPLIT",FACE,{"disambiguationData":[TD([subQ6,subQ11,subQ3,subQ1,subQ8,subQ9,subQ10])],"derivedFrom":subQ6}),makeQuery(id+"F98.boolean.opBoolean","SPLIT",FACE,{"disambiguationData":[TD([subQ6,subQ5,subQ3,subQ1,subQ8,subQ9,subQ10])],"derivedFrom":subQ6}),makeQuery(id+"F98.boolean.opBoolean","SPLIT",FACE,{"disambiguationData":[TD([subQ6,subQ11,subQ5,subQ3,subQ1,subQ8,subQ9,subQ10])],"derivedFrom":subQ6})],"fromTools":[makeQuery(id+"F101.opExtrude","SWEPT_FACE",FACE,{"disambiguationData":[OSD([sQuery(id+"F99.wireOp",EDGE,"E94")])]})]})}),makeQuery(id+"F104.opExtrude","SWEPT_FACE",FACE,{"disambiguationData":[OSD([sQuery(id+"F103.wireOp",EDGE,"E102")])]})]});}
            var Q22;
            {var subQ2=sQuery(id+"F97.wireOp",EDGE,"E90");var subQ3=sQuery(id+"F97.wireOp",EDGE,"E92");var subQ4=makeQuery(id+"F102.opExtrude","SWEPT_FACE",FACE,{"disambiguationData":[OSD([sQuery(id+"F100.wireOp",EDGE,"E97")])]});Q22=makeQuery(id+"F104.boolean.opBoolean","INTERSECT",EDGE,{"derivedFrom":[makeQuery(id+"F102.boolean.opBoolean","COPY",FACE,{"disambiguationData":[TD([makeQuery(id+"F98.opExtrude","CAP_FACE",FACE,{"disambiguationData":[OSD([subQ2,subQ3])],"isStart":false})])],"derivedFrom":subQ4}),makeQuery(id+"F104.opExtrude","SWEPT_FACE",FACE,{"disambiguationData":[OSD([sQuery(id+"F103.wireOp",EDGE,"E102")])]})]});}
            var Q23;
            Q23=makeQuery(id+"F104.boolean.opBoolean","INTERSECT",EDGE,{"derivedFrom":[makeQuery(id+"F98.opExtrude","CAP_FACE",FACE,{"disambiguationData":[OSD([sQuery(id+"F97.wireOp",EDGE,"E90"),sQuery(id+"F97.wireOp",EDGE,"E92")])],"isStart":false}),makeQuery(id+"F104.opExtrude","SWEPT_FACE",FACE,{"disambiguationData":[OSD([sQuery(id+"F103.wireOp",EDGE,"E102")])]})]});
            var Q24;
            {var subQ0=sQuery(id+"F97.wireOp",EDGE,"E90");var subQ1=makeQuery(id+"F98.opExtrude","SWEPT_FACE",FACE,{"disambiguationData":[OSD([subQ0])]});var subQ2=sQuery(id+"F94.wireOp",EDGE,"E86");var subQ3=makeQuery(id+"F95.opExtrude","SWEPT_FACE",FACE,{"disambiguationData":[OSD([subQ2])]});var subQ4=sQuery(id+"F94.wireOp",EDGE,"E84");var subQ5=makeQuery(id+"F95.opExtrude","CAP_FACE",FACE,{"disambiguationData":[OSD([subQ4,subQ2])],"isStart":false});var subQ6=makeQuery(id+"F95.opExtrude","SWEPT_FACE",FACE,{"disambiguationData":[OSD([subQ4])]});var subQ7=sQuery(id+"F97.wireOp",EDGE,"E92");var subQ8=makeQuery(id+"F98.opExtrude","CAP_FACE",FACE,{"disambiguationData":[OSD([subQ0,subQ7])],"isStart":true});var subQ9=makeQuery(id+"F98.opExtrude","CAP_FACE",FACE,{"disambiguationData":[OSD([subQ0,subQ7])],"isStart":false});var subQ10=makeQuery(id+"F98.opExtrude","SWEPT_FACE",FACE,{"disambiguationData":[OSD([subQ7])]});var subQ11=makeQuery(id+"F95.opExtrude","CAP_FACE",FACE,{"disambiguationData":[OSD([subQ4,subQ2])],"isStart":true});Q24=makeQuery(id+"F104.boolean.opBoolean","INTERSECT",EDGE,{"derivedFrom":[makeQuery(id+"F102.boolean.opBoolean","SPLIT",FACE,{"disambiguationData":[TD([subQ5])],"derivedFrom":makeQuery(id+"F101.boolean.opBoolean","MERGE",FACE,{"derivedFrom":[makeQuery(id+"F98.boolean.opBoolean","SPLIT",FACE,{"disambiguationData":[TD([subQ6,subQ11,subQ3,subQ1,subQ8,subQ9,subQ10])],"derivedFrom":subQ6}),makeQuery(id+"F98.boolean.opBoolean","SPLIT",FACE,{"disambiguationData":[TD([subQ6,subQ5,subQ3,subQ1,subQ8,subQ9,subQ10])],"derivedFrom":subQ6}),makeQuery(id+"F98.boolean.opBoolean","SPLIT",FACE,{"disambiguationData":[TD([subQ6,subQ11,subQ5,subQ3,subQ1,subQ8,subQ9,subQ10])],"derivedFrom":subQ6})],"fromTools":[makeQuery(id+"F101.opExtrude","SWEPT_FACE",FACE,{"disambiguationData":[OSD([sQuery(id+"F99.wireOp",EDGE,"E94")])]})]})}),makeQuery(id+"F104.opExtrude","SWEPT_FACE",FACE,{"disambiguationData":[OSD([sQuery(id+"F103.wireOp",EDGE,"E101")])]})]});}
            var Q25;
            Q25=makeQuery(id+"F104.boolean.opBoolean","INTERSECT",EDGE,{"derivedFrom":[makeQuery(id+"F95.opExtrude","CAP_FACE",FACE,{"disambiguationData":[OSD([sQuery(id+"F94.wireOp",EDGE,"E84"),sQuery(id+"F94.wireOp",EDGE,"E86")])],"isStart":false}),makeQuery(id+"F104.opExtrude","SWEPT_FACE",FACE,{"disambiguationData":[OSD([sQuery(id+"F103.wireOp",EDGE,"E101")])]})]});
            var Q26;
            Q26=makeQuery(id+"F104.boolean.opBoolean","INTERSECT",EDGE,{"derivedFrom":[makeQuery(id+"F95.opExtrude","CAP_FACE",FACE,{"disambiguationData":[OSD([sQuery(id+"F94.wireOp",EDGE,"E84"),sQuery(id+"F94.wireOp",EDGE,"E86")])],"isStart":false}),makeQuery(id+"F104.opExtrude","CAP_FACE",FACE,{"disambiguationData":[OSD([sQuery(id+"F103.wireOp",EDGE,"E101")])],"isStart":false})]});
            var Q27;
            {var subQ0=sQuery(id+"F97.wireOp",EDGE,"E90");var subQ1=sQuery(id+"F94.wireOp",EDGE,"E86");var subQ2=makeQuery(id+"F95.opExtrude","SWEPT_FACE",FACE,{"disambiguationData":[OSD([subQ1])]});var subQ3=sQuery(id+"F94.wireOp",EDGE,"E84");var subQ4=sQuery(id+"F97.wireOp",EDGE,"E92");Q27=makeQuery(id+"F104.boolean.opBoolean","INTERSECT",EDGE,{"derivedFrom":[makeQuery(id+"F98.boolean.opBoolean","SPLIT",FACE,{"disambiguationData":[TD([makeQuery(id+"F95.opExtrude","SWEPT_FACE",FACE,{"disambiguationData":[OSD([subQ3])]}),makeQuery(id+"F95.opExtrude","CAP_FACE",FACE,{"disambiguationData":[OSD([subQ3,subQ1])],"isStart":false}),subQ2,makeQuery(id+"F98.opExtrude","SWEPT_FACE",FACE,{"disambiguationData":[OSD([subQ0])]}),makeQuery(id+"F98.opExtrude","CAP_FACE",FACE,{"disambiguationData":[OSD([subQ0,subQ4])],"isStart":true}),makeQuery(id+"F98.opExtrude","CAP_FACE",FACE,{"disambiguationData":[OSD([subQ0,subQ4])],"isStart":false}),makeQuery(id+"F98.opExtrude","SWEPT_FACE",FACE,{"disambiguationData":[OSD([subQ4])]})])],"derivedFrom":subQ2}),makeQuery(id+"F104.opExtrude","CAP_FACE",FACE,{"disambiguationData":[OSD([sQuery(id+"F103.wireOp",EDGE,"E101")])],"isStart":false})]});}
            var Q28;
            {var subQ0=sQuery(id+"F94.wireOp",EDGE,"E86");var subQ1=sQuery(id+"F94.wireOp",EDGE,"E84");var subQ2=sQuery(id+"F97.wireOp",EDGE,"E90");var subQ3=sQuery(id+"F97.wireOp",EDGE,"E92");var subQ4=makeQuery(id+"F98.opExtrude","SWEPT_FACE",FACE,{"disambiguationData":[OSD([subQ3])]});Q28=makeQuery(id+"F104.boolean.opBoolean","INTERSECT",EDGE,{"derivedFrom":[makeQuery(id+"F98.boolean.opBoolean","SPLIT",FACE,{"disambiguationData":[TD([makeQuery(id+"F95.opExtrude","SWEPT_FACE",FACE,{"disambiguationData":[OSD([subQ1])]}),makeQuery(id+"F95.opExtrude","CAP_FACE",FACE,{"disambiguationData":[OSD([subQ1,subQ0])],"isStart":true}),makeQuery(id+"F95.opExtrude","CAP_FACE",FACE,{"disambiguationData":[OSD([subQ1,subQ0])],"isStart":false}),makeQuery(id+"F95.opExtrude","SWEPT_FACE",FACE,{"disambiguationData":[OSD([subQ0])]}),makeQuery(id+"F98.opExtrude","SWEPT_FACE",FACE,{"disambiguationData":[OSD([subQ2])]}),makeQuery(id+"F98.opExtrude","CAP_FACE",FACE,{"disambiguationData":[OSD([subQ2,subQ3])],"isStart":true}),makeQuery(id+"F98.opExtrude","CAP_FACE",FACE,{"disambiguationData":[OSD([subQ2,subQ3])],"isStart":false}),subQ4])],"derivedFrom":subQ4}),makeQuery(id+"F104.opExtrude","CAP_FACE",FACE,{"disambiguationData":[OSD([sQuery(id+"F103.wireOp",EDGE,"E101")])],"isStart":false})]});}
            var Q29;
            Q29=makeQuery(id+"F104.boolean.opBoolean","INTERSECT",EDGE,{"derivedFrom":[makeQuery(id+"F98.opExtrude","CAP_FACE",FACE,{"disambiguationData":[OSD([sQuery(id+"F97.wireOp",EDGE,"E90"),sQuery(id+"F97.wireOp",EDGE,"E92")])],"isStart":true}),makeQuery(id+"F104.opExtrude","CAP_FACE",FACE,{"disambiguationData":[OSD([sQuery(id+"F103.wireOp",EDGE,"E101")])],"isStart":false})]});
            var Q30;
            Q30=makeQuery(id+"F104.boolean.opBoolean","INTERSECT",EDGE,{"derivedFrom":[makeQuery(id+"F98.opExtrude","CAP_FACE",FACE,{"disambiguationData":[OSD([sQuery(id+"F97.wireOp",EDGE,"E90"),sQuery(id+"F97.wireOp",EDGE,"E92")])],"isStart":true}),makeQuery(id+"F104.opExtrude","SWEPT_FACE",FACE,{"disambiguationData":[OSD([sQuery(id+"F103.wireOp",EDGE,"E101")])]})]});
            var Q31;
            {var subQ2=sQuery(id+"F97.wireOp",EDGE,"E90");var subQ3=sQuery(id+"F97.wireOp",EDGE,"E92");var subQ4=makeQuery(id+"F102.opExtrude","SWEPT_FACE",FACE,{"disambiguationData":[OSD([sQuery(id+"F100.wireOp",EDGE,"E97")])]});Q31=makeQuery(id+"F104.boolean.opBoolean","INTERSECT",EDGE,{"derivedFrom":[makeQuery(id+"F102.boolean.opBoolean","COPY",FACE,{"disambiguationData":[TD([makeQuery(id+"F98.opExtrude","CAP_FACE",FACE,{"disambiguationData":[OSD([subQ2,subQ3])],"isStart":true})])],"derivedFrom":subQ4}),makeQuery(id+"F104.opExtrude","SWEPT_FACE",FACE,{"disambiguationData":[OSD([sQuery(id+"F103.wireOp",EDGE,"E101")])]})]});}
            fillet(context, id + "F105", {"entities" : qUnion([Q0, Q1, Q2, Q3, Q4, Q5, Q6, Q7, Q8, Q9, Q10, Q11, Q12, Q13, Q14, Q15, Q16, Q17, Q18, Q19, Q20, Q21, Q22, Q23, Q24, Q25, Q26, Q27, Q28, Q29, Q30, Q31]), "radius" : 1.5 * mm, "tangentPropagation" : true, "allowEdgeOverflow" : false});
        }
        {
            var Q0;
            {var subQ0=sQuery(id+"F94.wireOp",EDGE,"E86");var subQ1=sQuery(id+"F94.wireOp",EDGE,"E84");var subQ2=sQuery(id+"F97.wireOp",EDGE,"E90");var subQ3=makeQuery(id+"F98.opExtrude","SWEPT_FACE",FACE,{"disambiguationData":[OSD([subQ2])]});var subQ4=sQuery(id+"F97.wireOp",EDGE,"E92");Q0=makeQuery(id+"F104.boolean.opBoolean","INTERSECT",EDGE,{"derivedFrom":[makeQuery(id+"F98.boolean.opBoolean","SPLIT",FACE,{"disambiguationData":[TD([makeQuery(id+"F95.opExtrude","SWEPT_FACE",FACE,{"disambiguationData":[OSD([subQ1])]}),makeQuery(id+"F95.opExtrude","CAP_FACE",FACE,{"disambiguationData":[OSD([subQ1,subQ0])],"isStart":true}),makeQuery(id+"F95.opExtrude","CAP_FACE",FACE,{"disambiguationData":[OSD([subQ1,subQ0])],"isStart":false}),makeQuery(id+"F95.opExtrude","SWEPT_FACE",FACE,{"disambiguationData":[OSD([subQ0])]}),subQ3,makeQuery(id+"F98.opExtrude","CAP_FACE",FACE,{"disambiguationData":[OSD([subQ2,subQ4])],"isStart":true}),makeQuery(id+"F98.opExtrude","SWEPT_FACE",FACE,{"disambiguationData":[OSD([subQ4])]})])],"derivedFrom":subQ3}),makeQuery(id+"F104.opExtrude","SWEPT_FACE",FACE,{"disambiguationData":[OSD([sQuery(id+"F103.wireOp",EDGE,"E100")])]})]});}
            var Q1;
            {var subQ0=sQuery(id+"F94.wireOp",EDGE,"E86");var subQ1=sQuery(id+"F94.wireOp",EDGE,"E84");var subQ2=sQuery(id+"F97.wireOp",EDGE,"E90");var subQ3=makeQuery(id+"F98.opExtrude","SWEPT_FACE",FACE,{"disambiguationData":[OSD([subQ2])]});var subQ4=sQuery(id+"F97.wireOp",EDGE,"E92");Q1=makeQuery(id+"F104.boolean.opBoolean","INTERSECT",EDGE,{"derivedFrom":[makeQuery(id+"F98.boolean.opBoolean","SPLIT",FACE,{"disambiguationData":[TD([makeQuery(id+"F95.opExtrude","SWEPT_FACE",FACE,{"disambiguationData":[OSD([subQ1])]}),makeQuery(id+"F95.opExtrude","CAP_FACE",FACE,{"disambiguationData":[OSD([subQ1,subQ0])],"isStart":true}),makeQuery(id+"F95.opExtrude","CAP_FACE",FACE,{"disambiguationData":[OSD([subQ1,subQ0])],"isStart":false}),makeQuery(id+"F95.opExtrude","SWEPT_FACE",FACE,{"disambiguationData":[OSD([subQ0])]}),subQ3,makeQuery(id+"F98.opExtrude","CAP_FACE",FACE,{"disambiguationData":[OSD([subQ2,subQ4])],"isStart":false}),makeQuery(id+"F98.opExtrude","SWEPT_FACE",FACE,{"disambiguationData":[OSD([subQ4])]})])],"derivedFrom":subQ3}),makeQuery(id+"F104.opExtrude","SWEPT_FACE",FACE,{"disambiguationData":[OSD([sQuery(id+"F103.wireOp",EDGE,"E99")])]})]});}
            var Q2;
            {var subQ0=sQuery(id+"F94.wireOp",EDGE,"E86");var subQ1=sQuery(id+"F94.wireOp",EDGE,"E84");var subQ2=sQuery(id+"F97.wireOp",EDGE,"E90");var subQ3=makeQuery(id+"F98.opExtrude","SWEPT_FACE",FACE,{"disambiguationData":[OSD([subQ2])]});var subQ4=sQuery(id+"F97.wireOp",EDGE,"E92");Q2=makeQuery(id+"F104.boolean.opBoolean","INTERSECT",EDGE,{"derivedFrom":[makeQuery(id+"F98.boolean.opBoolean","SPLIT",FACE,{"disambiguationData":[TD([makeQuery(id+"F95.opExtrude","SWEPT_FACE",FACE,{"disambiguationData":[OSD([subQ1])]}),makeQuery(id+"F95.opExtrude","CAP_FACE",FACE,{"disambiguationData":[OSD([subQ1,subQ0])],"isStart":true}),makeQuery(id+"F95.opExtrude","CAP_FACE",FACE,{"disambiguationData":[OSD([subQ1,subQ0])],"isStart":false}),makeQuery(id+"F95.opExtrude","SWEPT_FACE",FACE,{"disambiguationData":[OSD([subQ0])]}),subQ3,makeQuery(id+"F98.opExtrude","CAP_FACE",FACE,{"disambiguationData":[OSD([subQ2,subQ4])],"isStart":false}),makeQuery(id+"F98.opExtrude","SWEPT_FACE",FACE,{"disambiguationData":[OSD([subQ4])]})])],"derivedFrom":subQ3}),makeQuery(id+"F104.opExtrude","SWEPT_FACE",FACE,{"disambiguationData":[OSD([sQuery(id+"F103.wireOp",EDGE,"E102")])]})]});}
            var Q3;
            {var subQ0=sQuery(id+"F94.wireOp",EDGE,"E86");var subQ1=sQuery(id+"F94.wireOp",EDGE,"E84");var subQ2=sQuery(id+"F97.wireOp",EDGE,"E90");var subQ3=makeQuery(id+"F98.opExtrude","SWEPT_FACE",FACE,{"disambiguationData":[OSD([subQ2])]});var subQ4=sQuery(id+"F97.wireOp",EDGE,"E92");Q3=makeQuery(id+"F104.boolean.opBoolean","INTERSECT",EDGE,{"derivedFrom":[makeQuery(id+"F98.boolean.opBoolean","SPLIT",FACE,{"disambiguationData":[TD([makeQuery(id+"F95.opExtrude","SWEPT_FACE",FACE,{"disambiguationData":[OSD([subQ1])]}),makeQuery(id+"F95.opExtrude","CAP_FACE",FACE,{"disambiguationData":[OSD([subQ1,subQ0])],"isStart":true}),makeQuery(id+"F95.opExtrude","CAP_FACE",FACE,{"disambiguationData":[OSD([subQ1,subQ0])],"isStart":false}),makeQuery(id+"F95.opExtrude","SWEPT_FACE",FACE,{"disambiguationData":[OSD([subQ0])]}),subQ3,makeQuery(id+"F98.opExtrude","CAP_FACE",FACE,{"disambiguationData":[OSD([subQ2,subQ4])],"isStart":true}),makeQuery(id+"F98.opExtrude","SWEPT_FACE",FACE,{"disambiguationData":[OSD([subQ4])]})])],"derivedFrom":subQ3}),makeQuery(id+"F104.opExtrude","SWEPT_FACE",FACE,{"disambiguationData":[OSD([sQuery(id+"F103.wireOp",EDGE,"E101")])]})]});}
            fillet(context, id + "F106", {"entities" : qUnion([Q0, Q1, Q2, Q3]), "radius" : 1.5 * mm, "tangentPropagation" : true, "allowEdgeOverflow" : false});
        }
        {
            var Q0;
            Q0=qCreatedBy(id+"F86.planeOp",FACE);
            var sketch = newSketch(context, id + "F107", { "sketchPlane" : qUnion([Q0])});
            skPoint(sketch, "E103", {"position": v(0, 60) * mm});
            skLineSegment(sketch, "E104.bottom", {"start": v(-25, 85) * mm, "end": v(25, 85) * mm});
            skLineSegment(sketch, "E104.top", {"start": v(-25, 35) * mm, "end": v(25, 35) * mm});
            skLineSegment(sketch, "E104.left", {"start": v(-25, 85) * mm, "end": v(-25, 35) * mm});
            skLineSegment(sketch, "E104.right", {"start": v(25, 85) * mm, "end": v(25, 35) * mm});
            skSolve(sketch);
        }
        {
            var Q0;
            Q0=makeQuery(id+"F107.imprint","IMPRINT",FACE,{"disambiguationData":[TD([[makeQuery(id+"F107.imprint","IMPRINT",EDGE,{"derivedFrom":sQuery(id+"F107.wireOp",EDGE,"E104.bottom")}),-1.0]])]});
            extrude(context, id + "F108", {"entities" : qUnion([Q0]), "oppositeDirection" : true, "depth" : 50 * mm, "offsetDistance" : 25 * mm});
        }
        {
            var Q0;
            Q0=qCreatedBy(makeId("Right.planeOp"),FACE);
            var sketch = newSketch(context, id + "F109", { "sketchPlane" : qUnion([Q0])});
            skPoint(sketch, "E105", {"position": v(-60, 0) * mm});
            skPoint(sketch, "E106", {"position": v(-60, 22.5) * mm});
            skPoint(sketch, "E107", {"position": v(-60, -22.5) * mm});
            skArc(sketch, "E108", {"start": v(-60, -22.5) * mm, "mid": v(-37.5, 0) * mm, "end": v(-60, 22.5) * mm});
            skLineSegment(sketch, "E109", {"start": v(-60, -22.5) * mm, "end": v(-60, 22.5) * mm});
            skSolve(sketch);
        }
        {
            var Q0;
            Q0 = qSketchRegion(id + "F109", true);
            var Q1;
            Q1=sQuery(id+"F109.wireOp",EDGE,"E109");
            revolve(context, id + "F110", {"operationType" : NewBodyOperationType.REMOVE, "surfaceOperationType" : NewSurfaceOperationType.NEW, "entities" : qUnion([Q0]), "axis" : qUnion([Q1]), "revolveType" : RevolveType.FULL, "oppositeDirection" : true});
        }
        {
            var Q0;
            Q0=makeQuery(id+"F108.opExtrude","SWEPT_FACE",FACE,{"disambiguationData":[OSD([sQuery(id+"F107.wireOp",EDGE,"E104.right")])]});
            var sketch = newSketch(context, id + "F111", { "sketchPlane" : qUnion([Q0])});
            skPoint(sketch, "E110", {"position": v(-60, 0) * mm});
            skCircle(sketch, "E111", {"center": v(-60, 0) * mm, "radius": 20 * mm});
            skSolve(sketch);
        }
        {
            var Q0;
            Q0=makeQuery(id+"F108.opExtrude","SWEPT_FACE",FACE,{"disambiguationData":[OSD([sQuery(id+"F107.wireOp",EDGE,"E104.bottom")])]});
            var sketch = newSketch(context, id + "F112", { "sketchPlane" : qUnion([Q0])});
            skPoint(sketch, "E112", {"position": v(0, 0) * mm});
            skCircle(sketch, "E113", {"center": v(0, 0) * mm, "radius": 20 * mm});
            skSolve(sketch);
        }
        {
            var Q0;
            Q0=makeQuery(id+"F108.opExtrude","CAP_FACE",FACE,{"disambiguationData":[OSD([sQuery(id+"F107.wireOp",EDGE,"E104.bottom"),sQuery(id+"F107.wireOp",EDGE,"E104.top"),sQuery(id+"F107.wireOp",EDGE,"E104.left"),sQuery(id+"F107.wireOp",EDGE,"E104.right")])],"isStart":false});
            var sketch = newSketch(context, id + "F113", { "sketchPlane" : qUnion([Q0])});
            skPoint(sketch, "E114", {"position": v(0, -60) * mm});
            skCircle(sketch, "E115", {"center": v(0, -60) * mm, "radius": 20 * mm});
            skSolve(sketch);
        }
        {
            var Q0;
            Q0=makeQuery(id+"F111.imprint","IMPRINT",FACE,{"disambiguationData":[TD([[makeQuery(id+"F111.imprint","IMPRINT",EDGE,{"derivedFrom":sQuery(id+"F111.wireOp",EDGE,"E111")}),1.0]])]});
            extrude(context, id + "F114", {"entities" : qUnion([Q0]), "operationType" : NewBodyOperationType.REMOVE, "oppositeDirection" : true, "depth" : 55 * mm, "offsetDistance" : 25 * mm});
        }
        {
            var Q0;
            Q0=makeQuery(id+"F113.imprint","IMPRINT",FACE,{"disambiguationData":[TD([[makeQuery(id+"F113.imprint","IMPRINT",EDGE,{"derivedFrom":sQuery(id+"F113.wireOp",EDGE,"E115")}),1.0]])]});
            extrude(context, id + "F115", {"entities" : qUnion([Q0]), "operationType" : NewBodyOperationType.REMOVE, "oppositeDirection" : true, "depth" : 55 * mm, "offsetDistance" : 25 * mm});
        }
        {
            var Q0;
            Q0=makeQuery(id+"F112.imprint","IMPRINT",FACE,{"disambiguationData":[TD([[makeQuery(id+"F112.imprint","IMPRINT",EDGE,{"derivedFrom":sQuery(id+"F112.wireOp",EDGE,"E113")}),1.0]])]});
            extrude(context, id + "F116", {"entities" : qUnion([Q0]), "operationType" : NewBodyOperationType.REMOVE, "oppositeDirection" : true, "depth" : 55 * mm, "offsetDistance" : 25 * mm});
        }
        {
            var Q0;
            Q0=makeQuery(id+"F108.opExtrude","CAP_EDGE",EDGE,{"disambiguationData":[OSD([sQuery(id+"F107.wireOp",EDGE,"E104.right")])],"isStart":false});
            var Q1;
            Q1=makeQuery(id+"F108.opExtrude","CAP_EDGE",EDGE,{"disambiguationData":[OSD([sQuery(id+"F107.wireOp",EDGE,"E104.top")])],"isStart":false});
            var Q2;
            Q2=makeQuery(id+"F108.opExtrude","CAP_EDGE",EDGE,{"disambiguationData":[OSD([sQuery(id+"F107.wireOp",EDGE,"E104.left")])],"isStart":false});
            var Q3;
            Q3=makeQuery(id+"F108.opExtrude","CAP_EDGE",EDGE,{"disambiguationData":[OSD([sQuery(id+"F107.wireOp",EDGE,"E104.bottom")])],"isStart":false});
            var Q4;
            Q4=makeQuery(id+"F108.opExtrude","CAP_EDGE",EDGE,{"disambiguationData":[OSD([sQuery(id+"F107.wireOp",EDGE,"E104.right")])],"isStart":true});
            var Q5;
            Q5=makeQuery(id+"F108.opExtrude","CAP_EDGE",EDGE,{"disambiguationData":[OSD([sQuery(id+"F107.wireOp",EDGE,"E104.top")])],"isStart":true});
            var Q6;
            Q6=makeQuery(id+"F108.opExtrude","CAP_EDGE",EDGE,{"disambiguationData":[OSD([sQuery(id+"F107.wireOp",EDGE,"E104.left")])],"isStart":true});
            var Q7;
            Q7=makeQuery(id+"F108.opExtrude","CAP_EDGE",EDGE,{"disambiguationData":[OSD([sQuery(id+"F107.wireOp",EDGE,"E104.bottom")])],"isStart":true});
            var Q8;
            Q8=makeQuery(id+"F108.opExtrude","SWEPT_EDGE",EDGE,{"disambiguationData":[OSD([sQuery(id+"F107.wireOp",EDGE,"E104.bottom"),sQuery(id+"F107.wireOp",EDGE,"E104.right")])]});
            var Q9;
            Q9=makeQuery(id+"F108.opExtrude","SWEPT_EDGE",EDGE,{"disambiguationData":[OSD([sQuery(id+"F107.wireOp",EDGE,"E104.bottom"),sQuery(id+"F107.wireOp",EDGE,"E104.left")])]});
            var Q10;
            Q10=makeQuery(id+"F108.opExtrude","SWEPT_EDGE",EDGE,{"disambiguationData":[OSD([sQuery(id+"F107.wireOp",EDGE,"E104.top"),sQuery(id+"F107.wireOp",EDGE,"E104.left")])]});
            var Q11;
            Q11=makeQuery(id+"F108.opExtrude","SWEPT_EDGE",EDGE,{"disambiguationData":[OSD([sQuery(id+"F107.wireOp",EDGE,"E104.top"),sQuery(id+"F107.wireOp",EDGE,"E104.right")])]});
            var Q12;
            Q12=makeQuery(id+"F115.boolean.opBoolean","INTERSECT",EDGE,{"disambiguationData":[OD(0.0)],"derivedFrom":[makeQuery(id+"F114.boolean.opBoolean","COPY",FACE,{"disambiguationData":[TD([makeQuery(id+"F108.opExtrude","SWEPT_FACE",FACE,{"disambiguationData":[OSD([sQuery(id+"F107.wireOp",EDGE,"E104.left")])]})])],"derivedFrom":makeQuery(id+"F114.opExtrude","SWEPT_FACE",FACE,{"disambiguationData":[OSD([sQuery(id+"F111.wireOp",EDGE,"E111")])]})}),makeQuery(id+"F115.opExtrude","SWEPT_FACE",FACE,{"disambiguationData":[OSD([sQuery(id+"F113.wireOp",EDGE,"E115")])]})]});
            var Q13;
            {var subQ0=sQuery(id+"F107.wireOp",EDGE,"E104.right");var subQ1=sQuery(id+"F107.wireOp",EDGE,"E104.left");Q13=makeQuery(id+"F116.boolean.opBoolean","INTERSECT",EDGE,{"disambiguationData":[OD(1.0)],"derivedFrom":[makeQuery(id+"F115.boolean.opBoolean","COPY",FACE,{"disambiguationData":[TD([makeQuery(id+"F108.opExtrude","CAP_FACE",FACE,{"disambiguationData":[OSD([sQuery(id+"F107.wireOp",EDGE,"E104.bottom"),sQuery(id+"F107.wireOp",EDGE,"E104.top"),subQ1,subQ0])],"isStart":false})])],"derivedFrom":makeQuery(id+"F115.opExtrude","SWEPT_FACE",FACE,{"disambiguationData":[OSD([sQuery(id+"F113.wireOp",EDGE,"E115")])]})}),makeQuery(id+"F116.opExtrude","SWEPT_FACE",FACE,{"disambiguationData":[OSD([sQuery(id+"F112.wireOp",EDGE,"E113")])]})]});}
            var Q14;
            Q14=makeQuery(id+"F116.boolean.opBoolean","INTERSECT",EDGE,{"disambiguationData":[OD(1.0)],"derivedFrom":[makeQuery(id+"F114.boolean.opBoolean","COPY",FACE,{"disambiguationData":[TD([makeQuery(id+"F108.opExtrude","SWEPT_FACE",FACE,{"disambiguationData":[OSD([sQuery(id+"F107.wireOp",EDGE,"E104.left")])]})])],"derivedFrom":makeQuery(id+"F114.opExtrude","SWEPT_FACE",FACE,{"disambiguationData":[OSD([sQuery(id+"F111.wireOp",EDGE,"E111")])]})}),makeQuery(id+"F116.opExtrude","SWEPT_FACE",FACE,{"disambiguationData":[OSD([sQuery(id+"F112.wireOp",EDGE,"E113")])]})]});
            var Q15;
            Q15=makeQuery(id+"F115.boolean.opBoolean","INTERSECT",EDGE,{"disambiguationData":[OD(1.0)],"derivedFrom":[makeQuery(id+"F114.boolean.opBoolean","COPY",FACE,{"disambiguationData":[TD([makeQuery(id+"F108.opExtrude","SWEPT_FACE",FACE,{"disambiguationData":[OSD([sQuery(id+"F107.wireOp",EDGE,"E104.left")])]})])],"derivedFrom":makeQuery(id+"F114.opExtrude","SWEPT_FACE",FACE,{"disambiguationData":[OSD([sQuery(id+"F111.wireOp",EDGE,"E111")])]})}),makeQuery(id+"F115.opExtrude","SWEPT_FACE",FACE,{"disambiguationData":[OSD([sQuery(id+"F113.wireOp",EDGE,"E115")])]})]});
            var Q16;
            Q16=makeQuery(id+"F116.boolean.opBoolean","INTERSECT",EDGE,{"disambiguationData":[OD(0.0)],"derivedFrom":[makeQuery(id+"F114.boolean.opBoolean","COPY",FACE,{"disambiguationData":[TD([makeQuery(id+"F108.opExtrude","SWEPT_FACE",FACE,{"disambiguationData":[OSD([sQuery(id+"F107.wireOp",EDGE,"E104.left")])]})])],"derivedFrom":makeQuery(id+"F114.opExtrude","SWEPT_FACE",FACE,{"disambiguationData":[OSD([sQuery(id+"F111.wireOp",EDGE,"E111")])]})}),makeQuery(id+"F116.opExtrude","SWEPT_FACE",FACE,{"disambiguationData":[OSD([sQuery(id+"F112.wireOp",EDGE,"E113")])]})]});
            var Q17;
            {var subQ0=sQuery(id+"F107.wireOp",EDGE,"E104.right");var subQ1=sQuery(id+"F107.wireOp",EDGE,"E104.left");Q17=makeQuery(id+"F116.boolean.opBoolean","INTERSECT",EDGE,{"disambiguationData":[OD(1.0)],"derivedFrom":[makeQuery(id+"F115.boolean.opBoolean","COPY",FACE,{"disambiguationData":[TD([makeQuery(id+"F108.opExtrude","CAP_FACE",FACE,{"disambiguationData":[OSD([sQuery(id+"F107.wireOp",EDGE,"E104.bottom"),sQuery(id+"F107.wireOp",EDGE,"E104.top"),subQ1,subQ0])],"isStart":true})])],"derivedFrom":makeQuery(id+"F115.opExtrude","SWEPT_FACE",FACE,{"disambiguationData":[OSD([sQuery(id+"F113.wireOp",EDGE,"E115")])]})}),makeQuery(id+"F116.opExtrude","SWEPT_FACE",FACE,{"disambiguationData":[OSD([sQuery(id+"F112.wireOp",EDGE,"E113")])]})]});}
            var Q18;
            {var subQ0=sQuery(id+"F107.wireOp",EDGE,"E104.right");var subQ1=sQuery(id+"F107.wireOp",EDGE,"E104.left");Q18=makeQuery(id+"F116.boolean.opBoolean","INTERSECT",EDGE,{"disambiguationData":[OD(0.0)],"derivedFrom":[makeQuery(id+"F115.boolean.opBoolean","COPY",FACE,{"disambiguationData":[TD([makeQuery(id+"F108.opExtrude","CAP_FACE",FACE,{"disambiguationData":[OSD([sQuery(id+"F107.wireOp",EDGE,"E104.bottom"),sQuery(id+"F107.wireOp",EDGE,"E104.top"),subQ1,subQ0])],"isStart":true})])],"derivedFrom":makeQuery(id+"F115.opExtrude","SWEPT_FACE",FACE,{"disambiguationData":[OSD([sQuery(id+"F113.wireOp",EDGE,"E115")])]})}),makeQuery(id+"F116.opExtrude","SWEPT_FACE",FACE,{"disambiguationData":[OSD([sQuery(id+"F112.wireOp",EDGE,"E113")])]})]});}
            var Q19;
            {var subQ0=sQuery(id+"F107.wireOp",EDGE,"E104.right");var subQ1=sQuery(id+"F107.wireOp",EDGE,"E104.left");Q19=makeQuery(id+"F116.boolean.opBoolean","INTERSECT",EDGE,{"disambiguationData":[OD(0.0)],"derivedFrom":[makeQuery(id+"F115.boolean.opBoolean","COPY",FACE,{"disambiguationData":[TD([makeQuery(id+"F108.opExtrude","CAP_FACE",FACE,{"disambiguationData":[OSD([sQuery(id+"F107.wireOp",EDGE,"E104.bottom"),sQuery(id+"F107.wireOp",EDGE,"E104.top"),subQ1,subQ0])],"isStart":false})])],"derivedFrom":makeQuery(id+"F115.opExtrude","SWEPT_FACE",FACE,{"disambiguationData":[OSD([sQuery(id+"F113.wireOp",EDGE,"E115")])]})}),makeQuery(id+"F116.opExtrude","SWEPT_FACE",FACE,{"disambiguationData":[OSD([sQuery(id+"F112.wireOp",EDGE,"E113")])]})]});}
            var Q20;
            Q20=makeQuery(id+"F116.boolean.opBoolean","INTERSECT",EDGE,{"disambiguationData":[OD(0.0)],"derivedFrom":[makeQuery(id+"F114.boolean.opBoolean","COPY",FACE,{"disambiguationData":[TD([makeQuery(id+"F108.opExtrude","SWEPT_FACE",FACE,{"disambiguationData":[OSD([sQuery(id+"F107.wireOp",EDGE,"E104.right")])]})])],"derivedFrom":makeQuery(id+"F114.opExtrude","SWEPT_FACE",FACE,{"disambiguationData":[OSD([sQuery(id+"F111.wireOp",EDGE,"E111")])]})}),makeQuery(id+"F116.opExtrude","SWEPT_FACE",FACE,{"disambiguationData":[OSD([sQuery(id+"F112.wireOp",EDGE,"E113")])]})]});
            var Q21;
            Q21=makeQuery(id+"F115.boolean.opBoolean","INTERSECT",EDGE,{"disambiguationData":[OD(1.0)],"derivedFrom":[makeQuery(id+"F114.boolean.opBoolean","COPY",FACE,{"disambiguationData":[TD([makeQuery(id+"F108.opExtrude","SWEPT_FACE",FACE,{"disambiguationData":[OSD([sQuery(id+"F107.wireOp",EDGE,"E104.right")])]})])],"derivedFrom":makeQuery(id+"F114.opExtrude","SWEPT_FACE",FACE,{"disambiguationData":[OSD([sQuery(id+"F111.wireOp",EDGE,"E111")])]})}),makeQuery(id+"F115.opExtrude","SWEPT_FACE",FACE,{"disambiguationData":[OSD([sQuery(id+"F113.wireOp",EDGE,"E115")])]})]});
            var Q22;
            Q22=makeQuery(id+"F116.boolean.opBoolean","INTERSECT",EDGE,{"disambiguationData":[OD(1.0)],"derivedFrom":[makeQuery(id+"F114.boolean.opBoolean","COPY",FACE,{"disambiguationData":[TD([makeQuery(id+"F108.opExtrude","SWEPT_FACE",FACE,{"disambiguationData":[OSD([sQuery(id+"F107.wireOp",EDGE,"E104.right")])]})])],"derivedFrom":makeQuery(id+"F114.opExtrude","SWEPT_FACE",FACE,{"disambiguationData":[OSD([sQuery(id+"F111.wireOp",EDGE,"E111")])]})}),makeQuery(id+"F116.opExtrude","SWEPT_FACE",FACE,{"disambiguationData":[OSD([sQuery(id+"F112.wireOp",EDGE,"E113")])]})]});
            var Q23;
            Q23=makeQuery(id+"F115.boolean.opBoolean","INTERSECT",EDGE,{"disambiguationData":[OD(0.0)],"derivedFrom":[makeQuery(id+"F114.boolean.opBoolean","COPY",FACE,{"disambiguationData":[TD([makeQuery(id+"F108.opExtrude","SWEPT_FACE",FACE,{"disambiguationData":[OSD([sQuery(id+"F107.wireOp",EDGE,"E104.right")])]})])],"derivedFrom":makeQuery(id+"F114.opExtrude","SWEPT_FACE",FACE,{"disambiguationData":[OSD([sQuery(id+"F111.wireOp",EDGE,"E111")])]})}),makeQuery(id+"F115.opExtrude","SWEPT_FACE",FACE,{"disambiguationData":[OSD([sQuery(id+"F113.wireOp",EDGE,"E115")])]})]});
            var Q24;
            Q24=makeQuery(id+"F116.boolean.opBoolean","COPY",EDGE,{"derivedFrom":makeQuery(id+"F116.opExtrude","CAP_EDGE",EDGE,{"disambiguationData":[OSD([sQuery(id+"F112.wireOp",EDGE,"E113")])],"isStart":true})});
            var Q25;
            Q25=makeQuery(id+"F114.boolean.opBoolean","COPY",EDGE,{"derivedFrom":makeQuery(id+"F114.opExtrude","CAP_EDGE",EDGE,{"disambiguationData":[OSD([sQuery(id+"F111.wireOp",EDGE,"E111")])],"isStart":true})});
            var Q26;
            Q26=makeQuery(id+"F115.boolean.opBoolean","COPY",EDGE,{"derivedFrom":makeQuery(id+"F115.opExtrude","CAP_EDGE",EDGE,{"disambiguationData":[OSD([sQuery(id+"F113.wireOp",EDGE,"E115")])],"isStart":true})});
            var Q27;
            Q27=makeQuery(id+"F115.boolean.opBoolean","INTERSECT",EDGE,{"derivedFrom":[makeQuery(id+"F108.opExtrude","CAP_FACE",FACE,{"disambiguationData":[OSD([sQuery(id+"F107.wireOp",EDGE,"E104.bottom"),sQuery(id+"F107.wireOp",EDGE,"E104.top"),sQuery(id+"F107.wireOp",EDGE,"E104.left"),sQuery(id+"F107.wireOp",EDGE,"E104.right")])],"isStart":true}),makeQuery(id+"F115.opExtrude","SWEPT_FACE",FACE,{"disambiguationData":[OSD([sQuery(id+"F113.wireOp",EDGE,"E115")])]})]});
            var Q28;
            Q28=makeQuery(id+"F116.boolean.opBoolean","INTERSECT",EDGE,{"derivedFrom":[makeQuery(id+"F108.opExtrude","SWEPT_FACE",FACE,{"disambiguationData":[OSD([sQuery(id+"F107.wireOp",EDGE,"E104.top")])]}),makeQuery(id+"F116.opExtrude","SWEPT_FACE",FACE,{"disambiguationData":[OSD([sQuery(id+"F112.wireOp",EDGE,"E113")])]})]});
            var Q29;
            Q29=makeQuery(id+"F114.boolean.opBoolean","INTERSECT",EDGE,{"derivedFrom":[makeQuery(id+"F108.opExtrude","SWEPT_FACE",FACE,{"disambiguationData":[OSD([sQuery(id+"F107.wireOp",EDGE,"E104.left")])]}),makeQuery(id+"F114.opExtrude","SWEPT_FACE",FACE,{"disambiguationData":[OSD([sQuery(id+"F111.wireOp",EDGE,"E111")])]})]});
            fillet(context, id + "F117", {"entities" : qUnion([Q0, Q1, Q2, Q3, Q4, Q5, Q6, Q7, Q8, Q9, Q10, Q11, Q12, Q13, Q14, Q15, Q16, Q17, Q18, Q19, Q20, Q21, Q22, Q23, Q24, Q25, Q26, Q27, Q28, Q29]), "radius" : 2.5 * mm, "tangentPropagation" : true, "allowEdgeOverflow" : false});
        }
        {
            var Q0;
            Q0=makeQuery(id+"F117.opFillet","SPLIT",FACE,{"disambiguationData":[OD(3.0)],"derivedFrom":makeQuery(id+"F108.opExtrude","CAP_FACE",FACE,{"disambiguationData":[OSD([sQuery(id+"F107.wireOp",EDGE,"E104.bottom"),sQuery(id+"F107.wireOp",EDGE,"E104.top"),sQuery(id+"F107.wireOp",EDGE,"E104.left"),sQuery(id+"F107.wireOp",EDGE,"E104.right")])],"isStart":false})});
            var sketch = newSketch(context, id + "F118", { "sketchPlane" : qUnion([Q0])});
            skPoint(sketch, "E116", {"position": v(16, -37.5) * mm});
            skPoint(sketch, "E117", {"position": v(22.5, -44) * mm});
            skPoint(sketch, "E118", {"position": v(-16, -37.5) * mm});
            skPoint(sketch, "E119", {"position": v(22.5, -76) * mm});
            skPoint(sketch, "E120", {"position": v(16, -82.5) * mm});
            skPoint(sketch, "E121", {"position": v(-16, -82.5) * mm});
            skPoint(sketch, "E122", {"position": v(-22.5, -44) * mm});
            skPoint(sketch, "E123", {"position": v(-22.5, -76) * mm});
            skLineSegment(sketch, "E124", {"start": v(-22.5, -44) * mm, "end": v(-16, -37.5) * mm});
            skLineSegment(sketch, "E125", {"start": v(16, -37.5) * mm, "end": v(22.5, -44) * mm});
            skLineSegment(sketch, "E126", {"start": v(22.5, -76) * mm, "end": v(16, -82.5) * mm});
            skLineSegment(sketch, "E127", {"start": v(-16, -82.5) * mm, "end": v(-22.5, -76) * mm});
            skSolve(sketch);
        }
        {
            var Q0;
            Q0=sQuery(id+"F118.wireOp",EDGE,"E125");
            cPlane(context, id + "F119", {"entities" : qUnion([Q0]), "cplaneType" : CPlaneType.LINE_ANGLE, "offset" : 25 * mm, "angle" : 135 * degree, "oppositeDirection" : true, "width" : 150 * mm, "height" : 150 * mm});
        }
        {
            var Q0;
            Q0=sQuery(id+"F118.wireOp",EDGE,"E124");
            cPlane(context, id + "F120", {"entities" : qUnion([Q0]), "cplaneType" : CPlaneType.LINE_ANGLE, "offset" : 25 * mm, "angle" : 45 * degree, "width" : 150 * mm, "height" : 150 * mm});
        }
        {
            var Q0;
            Q0=sQuery(id+"F118.wireOp",EDGE,"E127");
            cPlane(context, id + "F121", {"entities" : qUnion([Q0]), "cplaneType" : CPlaneType.LINE_ANGLE, "offset" : 25 * mm, "angle" : 45 * degree, "width" : 150 * mm, "height" : 150 * mm});
        }
        {
            var Q0;
            Q0=sQuery(id+"F118.wireOp",EDGE,"E126");
            cPlane(context, id + "F122", {"entities" : qUnion([Q0]), "cplaneType" : CPlaneType.LINE_ANGLE, "offset" : 25 * mm, "angle" : 45 * degree, "width" : 150 * mm, "height" : 150 * mm});
        }
        {
            var Q0;
            Q0=qCreatedBy(id+"F119.planeOp",FACE);
            var sketch = newSketch(context, id + "F123", { "sketchPlane" : qUnion([Q0])});
            skPoint(sketch, "E128", {"position": v(38.64, -18.84) * mm});
            skCircle(sketch, "E129", {"center": v(38.64, -18.84) * mm, "radius": 4.5 * mm});
            skSolve(sketch);
        }
        {
            var Q0;
            Q0=qCreatedBy(id+"F120.planeOp",FACE);
            var sketch = newSketch(context, id + "F124", { "sketchPlane" : qUnion([Q0])});
            skPoint(sketch, "E130", {"position": v(-38.64, -18.84) * mm});
            skCircle(sketch, "E131", {"center": v(-38.64, -18.84) * mm, "radius": 4.5 * mm});
            skSolve(sketch);
        }
        {
            var Q0;
            Q0=qCreatedBy(id+"F121.planeOp",FACE);
            var sketch = newSketch(context, id + "F125", { "sketchPlane" : qUnion([Q0])});
            skPoint(sketch, "E132", {"position": v(-4, -79.14) * mm});
            skCircle(sketch, "E133", {"center": v(-4, -79.14) * mm, "radius": 4.5 * mm});
            skSolve(sketch);
        }
        {
            var Q0;
            Q0=qCreatedBy(id+"F122.planeOp",FACE);
            var sketch = newSketch(context, id + "F126", { "sketchPlane" : qUnion([Q0])});
            skPoint(sketch, "E134", {"position": v(4, 79.14) * mm});
            skCircle(sketch, "E135", {"center": v(4, 79.14) * mm, "radius": 4.5 * mm});
            skSolve(sketch);
        }
        {
            var Q0;
            Q0=makeQuery(id+"F117.opFillet","SPLIT",FACE,{"disambiguationData":[OD(0.0)],"derivedFrom":makeQuery(id+"F108.opExtrude","CAP_FACE",FACE,{"disambiguationData":[OSD([sQuery(id+"F107.wireOp",EDGE,"E104.bottom"),sQuery(id+"F107.wireOp",EDGE,"E104.top"),sQuery(id+"F107.wireOp",EDGE,"E104.left"),sQuery(id+"F107.wireOp",EDGE,"E104.right")])],"isStart":false})});
            cPlane(context, id + "F127", {"entities" : qUnion([Q0]), "cplaneType" : CPlaneType.OFFSET, "offset" : 50 * mm, "width" : 150 * mm, "height" : 150 * mm});
        }
        {
            var Q0;
            Q0=qCreatedBy(id+"F127.planeOp",FACE);
            var sketch = newSketch(context, id + "F128", { "sketchPlane" : qUnion([Q0])});
            skPoint(sketch, "E136", {"position": v(0, -60) * mm});
            skLineSegment(sketch, "E137.bottom", {"start": v(-25, -85) * mm, "end": v(25, -85) * mm});
            skLineSegment(sketch, "E137.top", {"start": v(-25, -35) * mm, "end": v(25, -35) * mm});
            skLineSegment(sketch, "E137.left", {"start": v(-25, -85) * mm, "end": v(-25, -35) * mm});
            skLineSegment(sketch, "E137.right", {"start": v(25, -85) * mm, "end": v(25, -35) * mm});
            skSolve(sketch);
        }
        {
            var Q0;
            Q0 = qSketchRegion(id + "F128", true);
            extrude(context, id + "F129", {"entities" : qUnion([Q0]), "operationType" : NewBodyOperationType.ADD, "depth" : 50 * mm, "offsetDistance" : 25 * mm});
        }
        {
            var Q0;
            Q0=qCreatedBy(makeId("Right.planeOp"),FACE);
            var sketch = newSketch(context, id + "F130", { "sketchPlane" : qUnion([Q0])});
            skPoint(sketch, "E138", {"position": v(-60, 100) * mm});
            skPoint(sketch, "E139", {"position": v(-60, 77.5) * mm});
            skArc(sketch, "E140", {"start": v(-60, 77.5) * mm, "mid": v(-37.5, 100) * mm, "end": v(-60, 122.5) * mm});
            skLineSegment(sketch, "E141", {"start": v(-60, 122.5) * mm, "end": v(-60, 77.5) * mm});
            skSolve(sketch);
        }
        {
            var Q0;
            Q0 = qSketchRegion(id + "F130", true);
            var Q1;
            Q1=sQuery(id+"F130.wireOp",EDGE,"E141");
            revolve(context, id + "F131", {"operationType" : NewBodyOperationType.REMOVE, "surfaceOperationType" : NewSurfaceOperationType.NEW, "entities" : qUnion([Q0]), "axis" : qUnion([Q1]), "revolveType" : RevolveType.FULL, "oppositeDirection" : true});
        }
        {
            var Q0;
            Q0=makeQuery(id+"F129.opExtrude","SWEPT_FACE",FACE,{"disambiguationData":[OSD([sQuery(id+"F128.wireOp",EDGE,"E137.right")])]});
            var sketch = newSketch(context, id + "F132", { "sketchPlane" : qUnion([Q0])});
            skPoint(sketch, "E142", {"position": v(-60, 100) * mm});
            skCircle(sketch, "E143", {"center": v(-60, 100) * mm, "radius": 20 * mm});
            skSolve(sketch);
        }
        {
            var Q0;
            Q0=makeQuery(id+"F129.opExtrude","SWEPT_FACE",FACE,{"disambiguationData":[OSD([sQuery(id+"F128.wireOp",EDGE,"E137.bottom")])]});
            var sketch = newSketch(context, id + "F133", { "sketchPlane" : qUnion([Q0])});
            skPoint(sketch, "E144", {"position": v(0, 100) * mm});
            skCircle(sketch, "E145", {"center": v(0, 100) * mm, "radius": 20 * mm});
            skPoint(sketch, "E146", {"position": v(-906.02, -1225.95) * mm});
            skSolve(sketch);
        }
        {
            var Q0;
            Q0=makeQuery(id+"F129.opExtrude","CAP_FACE",FACE,{"disambiguationData":[OSD([sQuery(id+"F128.wireOp",EDGE,"E137.bottom"),sQuery(id+"F128.wireOp",EDGE,"E137.top"),sQuery(id+"F128.wireOp",EDGE,"E137.left"),sQuery(id+"F128.wireOp",EDGE,"E137.right")])],"isStart":false});
            var sketch = newSketch(context, id + "F134", { "sketchPlane" : qUnion([Q0])});
            skPoint(sketch, "E147", {"position": v(0, -60) * mm});
            skCircle(sketch, "E148", {"center": v(0, -60) * mm, "radius": 20 * mm});
            skSolve(sketch);
        }
        {
            var Q0;
            Q0=makeQuery(id+"F132.imprint","IMPRINT",FACE,{"disambiguationData":[TD([[makeQuery(id+"F132.imprint","IMPRINT",EDGE,{"derivedFrom":sQuery(id+"F132.wireOp",EDGE,"E143")}),1.0]])]});
            extrude(context, id + "F135", {"entities" : qUnion([Q0]), "operationType" : NewBodyOperationType.REMOVE, "oppositeDirection" : true, "depth" : 51 * mm, "offsetDistance" : 25 * mm});
        }
        {
            var Q0;
            Q0=makeQuery(id+"F134.imprint","IMPRINT",FACE,{"disambiguationData":[TD([[makeQuery(id+"F134.imprint","IMPRINT",EDGE,{"derivedFrom":sQuery(id+"F134.wireOp",EDGE,"E148")}),1.0]])]});
            extrude(context, id + "F136", {"entities" : qUnion([Q0]), "operationType" : NewBodyOperationType.REMOVE, "oppositeDirection" : true, "depth" : 51 * mm, "offsetDistance" : 25 * mm});
        }
        {
            var Q0;
            Q0=makeQuery(id+"F133.imprint","IMPRINT",FACE,{"disambiguationData":[TD([[makeQuery(id+"F133.imprint","IMPRINT",EDGE,{"derivedFrom":sQuery(id+"F133.wireOp",EDGE,"E145")}),1.0]])]});
            extrude(context, id + "F137", {"entities" : qUnion([Q0]), "operationType" : NewBodyOperationType.REMOVE, "oppositeDirection" : true, "depth" : 51 * mm, "offsetDistance" : 25 * mm});
        }
        {
            var Q0;
            Q0=makeQuery(id+"F129.opExtrude","CAP_EDGE",EDGE,{"disambiguationData":[OSD([sQuery(id+"F128.wireOp",EDGE,"E137.right")])],"isStart":false});
            var Q1;
            Q1=makeQuery(id+"F129.opExtrude","CAP_EDGE",EDGE,{"disambiguationData":[OSD([sQuery(id+"F128.wireOp",EDGE,"E137.top")])],"isStart":false});
            var Q2;
            Q2=makeQuery(id+"F129.opExtrude","CAP_EDGE",EDGE,{"disambiguationData":[OSD([sQuery(id+"F128.wireOp",EDGE,"E137.left")])],"isStart":false});
            var Q3;
            Q3=makeQuery(id+"F129.opExtrude","CAP_EDGE",EDGE,{"disambiguationData":[OSD([sQuery(id+"F128.wireOp",EDGE,"E137.bottom")])],"isStart":false});
            var Q4;
            Q4=makeQuery(id+"F129.opExtrude","CAP_EDGE",EDGE,{"disambiguationData":[OSD([sQuery(id+"F128.wireOp",EDGE,"E137.right")])],"isStart":true});
            var Q5;
            Q5=makeQuery(id+"F129.opExtrude","CAP_EDGE",EDGE,{"disambiguationData":[OSD([sQuery(id+"F128.wireOp",EDGE,"E137.bottom")])],"isStart":true});
            var Q6;
            Q6=makeQuery(id+"F129.opExtrude","CAP_EDGE",EDGE,{"disambiguationData":[OSD([sQuery(id+"F128.wireOp",EDGE,"E137.left")])],"isStart":true});
            var Q7;
            Q7=makeQuery(id+"F129.opExtrude","CAP_EDGE",EDGE,{"disambiguationData":[OSD([sQuery(id+"F128.wireOp",EDGE,"E137.top")])],"isStart":true});
            var Q8;
            Q8=makeQuery(id+"F129.opExtrude","SWEPT_EDGE",EDGE,{"disambiguationData":[OSD([sQuery(id+"F128.wireOp",EDGE,"E137.bottom"),sQuery(id+"F128.wireOp",EDGE,"E137.right")])]});
            var Q9;
            Q9=makeQuery(id+"F129.opExtrude","SWEPT_EDGE",EDGE,{"disambiguationData":[OSD([sQuery(id+"F128.wireOp",EDGE,"E137.top"),sQuery(id+"F128.wireOp",EDGE,"E137.right")])]});
            var Q10;
            Q10=makeQuery(id+"F129.opExtrude","SWEPT_EDGE",EDGE,{"disambiguationData":[OSD([sQuery(id+"F128.wireOp",EDGE,"E137.bottom"),sQuery(id+"F128.wireOp",EDGE,"E137.left")])]});
            var Q11;
            Q11=makeQuery(id+"F129.opExtrude","SWEPT_EDGE",EDGE,{"disambiguationData":[OSD([sQuery(id+"F128.wireOp",EDGE,"E137.top"),sQuery(id+"F128.wireOp",EDGE,"E137.left")])]});
            var Q12;
            Q12=makeQuery(id+"F136.boolean.opBoolean","COPY",EDGE,{"derivedFrom":makeQuery(id+"F136.opExtrude","CAP_EDGE",EDGE,{"disambiguationData":[OSD([sQuery(id+"F134.wireOp",EDGE,"E148")])],"isStart":true})});
            var Q13;
            Q13=makeQuery(id+"F137.boolean.opBoolean","INTERSECT",EDGE,{"derivedFrom":[makeQuery(id+"F129.opExtrude","SWEPT_FACE",FACE,{"disambiguationData":[OSD([sQuery(id+"F128.wireOp",EDGE,"E137.top")])]}),makeQuery(id+"F137.opExtrude","SWEPT_FACE",FACE,{"disambiguationData":[OSD([sQuery(id+"F133.wireOp",EDGE,"E145")])]})]});
            var Q14;
            Q14=makeQuery(id+"F135.boolean.opBoolean","COPY",EDGE,{"derivedFrom":makeQuery(id+"F135.opExtrude","CAP_EDGE",EDGE,{"disambiguationData":[OSD([sQuery(id+"F132.wireOp",EDGE,"E143")])],"isStart":true})});
            var Q15;
            Q15=makeQuery(id+"F137.boolean.opBoolean","COPY",EDGE,{"derivedFrom":makeQuery(id+"F137.opExtrude","CAP_EDGE",EDGE,{"disambiguationData":[OSD([sQuery(id+"F133.wireOp",EDGE,"E145")])],"isStart":true})});
            var Q16;
            Q16=makeQuery(id+"F135.boolean.opBoolean","INTERSECT",EDGE,{"derivedFrom":[makeQuery(id+"F129.opExtrude","SWEPT_FACE",FACE,{"disambiguationData":[OSD([sQuery(id+"F128.wireOp",EDGE,"E137.left")])]}),makeQuery(id+"F135.opExtrude","SWEPT_FACE",FACE,{"disambiguationData":[OSD([sQuery(id+"F132.wireOp",EDGE,"E143")])]})]});
            var Q17;
            Q17=makeQuery(id+"F137.boolean.opBoolean","INTERSECT",EDGE,{"disambiguationData":[OD(1.0)],"derivedFrom":[makeQuery(id+"F135.boolean.opBoolean","COPY",FACE,{"disambiguationData":[TD([makeQuery(id+"F129.opExtrude","SWEPT_FACE",FACE,{"disambiguationData":[OSD([sQuery(id+"F128.wireOp",EDGE,"E137.right")])]})])],"derivedFrom":makeQuery(id+"F135.opExtrude","SWEPT_FACE",FACE,{"disambiguationData":[OSD([sQuery(id+"F132.wireOp",EDGE,"E143")])]})}),makeQuery(id+"F137.opExtrude","SWEPT_FACE",FACE,{"disambiguationData":[OSD([sQuery(id+"F133.wireOp",EDGE,"E145")])]})]});
            var Q18;
            {var subQ0=sQuery(id+"F128.wireOp",EDGE,"E137.right");var subQ1=sQuery(id+"F128.wireOp",EDGE,"E137.left");Q18=makeQuery(id+"F137.boolean.opBoolean","INTERSECT",EDGE,{"disambiguationData":[OD(1.0)],"derivedFrom":[makeQuery(id+"F136.boolean.opBoolean","COPY",FACE,{"disambiguationData":[TD([makeQuery(id+"F129.opExtrude","CAP_FACE",FACE,{"disambiguationData":[OSD([sQuery(id+"F128.wireOp",EDGE,"E137.bottom"),sQuery(id+"F128.wireOp",EDGE,"E137.top"),subQ1,subQ0])],"isStart":true})])],"derivedFrom":makeQuery(id+"F136.opExtrude","SWEPT_FACE",FACE,{"disambiguationData":[OSD([sQuery(id+"F134.wireOp",EDGE,"E148")])]})}),makeQuery(id+"F137.opExtrude","SWEPT_FACE",FACE,{"disambiguationData":[OSD([sQuery(id+"F133.wireOp",EDGE,"E145")])]})]});}
            var Q19;
            Q19=makeQuery(id+"F136.boolean.opBoolean","INTERSECT",EDGE,{"disambiguationData":[OD(1.0)],"derivedFrom":[makeQuery(id+"F135.boolean.opBoolean","COPY",FACE,{"disambiguationData":[TD([makeQuery(id+"F129.opExtrude","SWEPT_FACE",FACE,{"disambiguationData":[OSD([sQuery(id+"F128.wireOp",EDGE,"E137.left")])]})])],"derivedFrom":makeQuery(id+"F135.opExtrude","SWEPT_FACE",FACE,{"disambiguationData":[OSD([sQuery(id+"F132.wireOp",EDGE,"E143")])]})}),makeQuery(id+"F136.opExtrude","SWEPT_FACE",FACE,{"disambiguationData":[OSD([sQuery(id+"F134.wireOp",EDGE,"E148")])]})]});
            var Q20;
            {var subQ0=sQuery(id+"F128.wireOp",EDGE,"E137.right");var subQ1=sQuery(id+"F128.wireOp",EDGE,"E137.left");Q20=makeQuery(id+"F137.boolean.opBoolean","INTERSECT",EDGE,{"disambiguationData":[OD(0.0)],"derivedFrom":[makeQuery(id+"F136.boolean.opBoolean","COPY",FACE,{"disambiguationData":[TD([makeQuery(id+"F129.opExtrude","CAP_FACE",FACE,{"disambiguationData":[OSD([sQuery(id+"F128.wireOp",EDGE,"E137.bottom"),sQuery(id+"F128.wireOp",EDGE,"E137.top"),subQ1,subQ0])],"isStart":true})])],"derivedFrom":makeQuery(id+"F136.opExtrude","SWEPT_FACE",FACE,{"disambiguationData":[OSD([sQuery(id+"F134.wireOp",EDGE,"E148")])]})}),makeQuery(id+"F137.opExtrude","SWEPT_FACE",FACE,{"disambiguationData":[OSD([sQuery(id+"F133.wireOp",EDGE,"E145")])]})]});}
            var Q21;
            Q21=makeQuery(id+"F136.boolean.opBoolean","INTERSECT",EDGE,{"disambiguationData":[OD(0.0)],"derivedFrom":[makeQuery(id+"F135.boolean.opBoolean","COPY",FACE,{"disambiguationData":[TD([makeQuery(id+"F129.opExtrude","SWEPT_FACE",FACE,{"disambiguationData":[OSD([sQuery(id+"F128.wireOp",EDGE,"E137.left")])]})])],"derivedFrom":makeQuery(id+"F135.opExtrude","SWEPT_FACE",FACE,{"disambiguationData":[OSD([sQuery(id+"F132.wireOp",EDGE,"E143")])]})}),makeQuery(id+"F136.opExtrude","SWEPT_FACE",FACE,{"disambiguationData":[OSD([sQuery(id+"F134.wireOp",EDGE,"E148")])]})]});
            var Q22;
            {var subQ0=sQuery(id+"F128.wireOp",EDGE,"E137.right");var subQ1=sQuery(id+"F128.wireOp",EDGE,"E137.left");Q22=makeQuery(id+"F137.boolean.opBoolean","INTERSECT",EDGE,{"disambiguationData":[OD(0.0)],"derivedFrom":[makeQuery(id+"F136.boolean.opBoolean","COPY",FACE,{"disambiguationData":[TD([makeQuery(id+"F129.opExtrude","CAP_FACE",FACE,{"disambiguationData":[OSD([sQuery(id+"F128.wireOp",EDGE,"E137.bottom"),sQuery(id+"F128.wireOp",EDGE,"E137.top"),subQ1,subQ0])],"isStart":false})])],"derivedFrom":makeQuery(id+"F136.opExtrude","SWEPT_FACE",FACE,{"disambiguationData":[OSD([sQuery(id+"F134.wireOp",EDGE,"E148")])]})}),makeQuery(id+"F137.opExtrude","SWEPT_FACE",FACE,{"disambiguationData":[OSD([sQuery(id+"F133.wireOp",EDGE,"E145")])]})]});}
            var Q23;
            {var subQ0=sQuery(id+"F128.wireOp",EDGE,"E137.right");var subQ1=sQuery(id+"F128.wireOp",EDGE,"E137.left");Q23=makeQuery(id+"F137.boolean.opBoolean","INTERSECT",EDGE,{"disambiguationData":[OD(1.0)],"derivedFrom":[makeQuery(id+"F136.boolean.opBoolean","COPY",FACE,{"disambiguationData":[TD([makeQuery(id+"F129.opExtrude","CAP_FACE",FACE,{"disambiguationData":[OSD([sQuery(id+"F128.wireOp",EDGE,"E137.bottom"),sQuery(id+"F128.wireOp",EDGE,"E137.top"),subQ1,subQ0])],"isStart":false})])],"derivedFrom":makeQuery(id+"F136.opExtrude","SWEPT_FACE",FACE,{"disambiguationData":[OSD([sQuery(id+"F134.wireOp",EDGE,"E148")])]})}),makeQuery(id+"F137.opExtrude","SWEPT_FACE",FACE,{"disambiguationData":[OSD([sQuery(id+"F133.wireOp",EDGE,"E145")])]})]});}
            var Q24;
            Q24=makeQuery(id+"F136.boolean.opBoolean","INTERSECT",EDGE,{"disambiguationData":[OD(0.0)],"derivedFrom":[makeQuery(id+"F135.boolean.opBoolean","COPY",FACE,{"disambiguationData":[TD([makeQuery(id+"F129.opExtrude","SWEPT_FACE",FACE,{"disambiguationData":[OSD([sQuery(id+"F128.wireOp",EDGE,"E137.right")])]})])],"derivedFrom":makeQuery(id+"F135.opExtrude","SWEPT_FACE",FACE,{"disambiguationData":[OSD([sQuery(id+"F132.wireOp",EDGE,"E143")])]})}),makeQuery(id+"F136.opExtrude","SWEPT_FACE",FACE,{"disambiguationData":[OSD([sQuery(id+"F134.wireOp",EDGE,"E148")])]})]});
            var Q25;
            Q25=makeQuery(id+"F137.boolean.opBoolean","INTERSECT",EDGE,{"disambiguationData":[OD(1.0)],"derivedFrom":[makeQuery(id+"F135.boolean.opBoolean","COPY",FACE,{"disambiguationData":[TD([makeQuery(id+"F129.opExtrude","SWEPT_FACE",FACE,{"disambiguationData":[OSD([sQuery(id+"F128.wireOp",EDGE,"E137.left")])]})])],"derivedFrom":makeQuery(id+"F135.opExtrude","SWEPT_FACE",FACE,{"disambiguationData":[OSD([sQuery(id+"F132.wireOp",EDGE,"E143")])]})}),makeQuery(id+"F137.opExtrude","SWEPT_FACE",FACE,{"disambiguationData":[OSD([sQuery(id+"F133.wireOp",EDGE,"E145")])]})]});
            var Q26;
            Q26=makeQuery(id+"F137.boolean.opBoolean","INTERSECT",EDGE,{"disambiguationData":[OD(0.0)],"derivedFrom":[makeQuery(id+"F135.boolean.opBoolean","COPY",FACE,{"disambiguationData":[TD([makeQuery(id+"F129.opExtrude","SWEPT_FACE",FACE,{"disambiguationData":[OSD([sQuery(id+"F128.wireOp",EDGE,"E137.left")])]})])],"derivedFrom":makeQuery(id+"F135.opExtrude","SWEPT_FACE",FACE,{"disambiguationData":[OSD([sQuery(id+"F132.wireOp",EDGE,"E143")])]})}),makeQuery(id+"F137.opExtrude","SWEPT_FACE",FACE,{"disambiguationData":[OSD([sQuery(id+"F133.wireOp",EDGE,"E145")])]})]});
            var Q27;
            Q27=makeQuery(id+"F137.boolean.opBoolean","INTERSECT",EDGE,{"disambiguationData":[OD(0.0)],"derivedFrom":[makeQuery(id+"F135.boolean.opBoolean","COPY",FACE,{"disambiguationData":[TD([makeQuery(id+"F129.opExtrude","SWEPT_FACE",FACE,{"disambiguationData":[OSD([sQuery(id+"F128.wireOp",EDGE,"E137.right")])]})])],"derivedFrom":makeQuery(id+"F135.opExtrude","SWEPT_FACE",FACE,{"disambiguationData":[OSD([sQuery(id+"F132.wireOp",EDGE,"E143")])]})}),makeQuery(id+"F137.opExtrude","SWEPT_FACE",FACE,{"disambiguationData":[OSD([sQuery(id+"F133.wireOp",EDGE,"E145")])]})]});
            var Q28;
            Q28=makeQuery(id+"F136.boolean.opBoolean","INTERSECT",EDGE,{"derivedFrom":[makeQuery(id+"F129.opExtrude","CAP_FACE",FACE,{"disambiguationData":[OSD([sQuery(id+"F128.wireOp",EDGE,"E137.bottom"),sQuery(id+"F128.wireOp",EDGE,"E137.top"),sQuery(id+"F128.wireOp",EDGE,"E137.left"),sQuery(id+"F128.wireOp",EDGE,"E137.right")])],"isStart":true}),makeQuery(id+"F136.opExtrude","SWEPT_FACE",FACE,{"disambiguationData":[OSD([sQuery(id+"F134.wireOp",EDGE,"E148")])]})]});
            fillet(context, id + "F138", {"entities" : qUnion([Q0, Q1, Q2, Q3, Q4, Q5, Q6, Q7, Q8, Q9, Q10, Q11, Q12, Q13, Q14, Q15, Q16, Q17, Q18, Q19, Q20, Q21, Q22, Q23, Q24, Q25, Q26, Q27, Q28]), "radius" : 2.5 * mm, "tangentPropagation" : true, "allowEdgeOverflow" : false});
        }
        {
            var Q0;
            Q0 = qSketchRegion(id + "F123", true);
            extrude(context, id + "F139", {"entities" : qUnion([Q0]), "operationType" : NewBodyOperationType.ADD, "depth" : 71.01 * mm, "offsetDistance" : 25 * mm});
        }
        {
            var Q0;
            Q0=makeQuery(id+"F125.imprint","IMPRINT",FACE,{"disambiguationData":[TD([[makeQuery(id+"F125.imprint","IMPRINT",EDGE,{"derivedFrom":sQuery(id+"F125.wireOp",EDGE,"E133")}),1.0]])]});
            extrude(context, id + "F140", {"entities" : qUnion([Q0]), "operationType" : NewBodyOperationType.ADD, "depth" : 71.01 * mm, "offsetDistance" : 25 * mm});
        }
        {
            var Q0;
            Q0=makeQuery(id+"F124.imprint","IMPRINT",FACE,{"disambiguationData":[TD([[makeQuery(id+"F124.imprint","IMPRINT",EDGE,{"derivedFrom":sQuery(id+"F124.wireOp",EDGE,"E131")}),1.0]])]});
            extrude(context, id + "F141", {"entities" : qUnion([Q0]), "operationType" : NewBodyOperationType.ADD, "depth" : 71.01 * mm, "offsetDistance" : 25 * mm});
        }
        {
            var Q0;
            Q0=makeQuery(id+"F126.imprint","IMPRINT",FACE,{"disambiguationData":[TD([[makeQuery(id+"F126.imprint","IMPRINT",EDGE,{"derivedFrom":sQuery(id+"F126.wireOp",EDGE,"E135")}),1.0]])]});
            extrude(context, id + "F142", {"entities" : qUnion([Q0]), "operationType" : NewBodyOperationType.ADD, "oppositeDirection" : true, "depth" : 71.01 * mm, "offsetDistance" : 25 * mm});
        }
        {
            var Q0;
            Q0=makeQuery(id+"F142.opExtrude","CAP_FACE",FACE,{"disambiguationData":[OSD([sQuery(id+"F126.wireOp",EDGE,"E135")])],"isStart":true});
            var Q1;
            Q1=sQuery(id+"F118.wireOp",EDGE,"E126");
            revolve(context, id + "F143", {"operationType" : NewBodyOperationType.ADD, "surfaceOperationType" : NewSurfaceOperationType.NEW, "entities" : qUnion([Q0]), "axis" : qUnion([Q1]), "revolveType" : RevolveType.FULL});
        }
        {
            var Q0;
            Q0=makeQuery(id+"F139.opExtrude","CAP_FACE",FACE,{"disambiguationData":[OSD([sQuery(id+"F123.wireOp",EDGE,"E129")])],"isStart":true});
            var Q1;
            Q1=makeQuery(id+"F139.boolean.opBoolean","INTERSECT",EDGE,{"derivedFrom":[makeQuery(id+"F117.opFillet","SPLIT",FACE,{"disambiguationData":[OD(3.0)],"derivedFrom":makeQuery(id+"F108.opExtrude","CAP_FACE",FACE,{"disambiguationData":[OSD([sQuery(id+"F107.wireOp",EDGE,"E104.bottom"),sQuery(id+"F107.wireOp",EDGE,"E104.top"),sQuery(id+"F107.wireOp",EDGE,"E104.left"),sQuery(id+"F107.wireOp",EDGE,"E104.right")])],"isStart":false})}),makeQuery(id+"F139.opExtrude","CAP_FACE",FACE,{"disambiguationData":[OSD([sQuery(id+"F123.wireOp",EDGE,"E129")])],"isStart":true})]});
            revolve(context, id + "F144", {"operationType" : NewBodyOperationType.ADD, "surfaceOperationType" : NewSurfaceOperationType.NEW, "entities" : qUnion([Q0]), "axis" : qUnion([Q1]), "revolveType" : RevolveType.FULL});
        }
        {
            var Q0;
            Q0=makeQuery(id+"F140.opExtrude","CAP_FACE",FACE,{"disambiguationData":[OSD([sQuery(id+"F125.wireOp",EDGE,"E133")])],"isStart":true});
            var Q1;
            Q1=makeQuery(id+"F140.boolean.opBoolean","INTERSECT",EDGE,{"derivedFrom":[makeQuery(id+"F117.opFillet","SPLIT",FACE,{"disambiguationData":[OD(0.0)],"derivedFrom":makeQuery(id+"F108.opExtrude","CAP_FACE",FACE,{"disambiguationData":[OSD([sQuery(id+"F107.wireOp",EDGE,"E104.bottom"),sQuery(id+"F107.wireOp",EDGE,"E104.top"),sQuery(id+"F107.wireOp",EDGE,"E104.left"),sQuery(id+"F107.wireOp",EDGE,"E104.right")])],"isStart":false})}),makeQuery(id+"F140.opExtrude","CAP_FACE",FACE,{"disambiguationData":[OSD([sQuery(id+"F125.wireOp",EDGE,"E133")])],"isStart":true})]});
            revolve(context, id + "F145", {"operationType" : NewBodyOperationType.ADD, "surfaceOperationType" : NewSurfaceOperationType.NEW, "entities" : qUnion([Q0]), "axis" : qUnion([Q1]), "revolveType" : RevolveType.FULL});
        }
        {
            var Q0;
            Q0=makeQuery(id+"F141.opExtrude","CAP_FACE",FACE,{"disambiguationData":[OSD([sQuery(id+"F124.wireOp",EDGE,"E131")])],"isStart":true});
            var Q1;
            Q1=makeQuery(id+"F141.boolean.opBoolean","INTERSECT",EDGE,{"derivedFrom":[makeQuery(id+"F117.opFillet","SPLIT",FACE,{"disambiguationData":[OD(2.0)],"derivedFrom":makeQuery(id+"F108.opExtrude","CAP_FACE",FACE,{"disambiguationData":[OSD([sQuery(id+"F107.wireOp",EDGE,"E104.bottom"),sQuery(id+"F107.wireOp",EDGE,"E104.top"),sQuery(id+"F107.wireOp",EDGE,"E104.left"),sQuery(id+"F107.wireOp",EDGE,"E104.right")])],"isStart":false})}),makeQuery(id+"F141.opExtrude","CAP_FACE",FACE,{"disambiguationData":[OSD([sQuery(id+"F124.wireOp",EDGE,"E131")])],"isStart":true})]});
            revolve(context, id + "F146", {"operationType" : NewBodyOperationType.ADD, "surfaceOperationType" : NewSurfaceOperationType.NEW, "entities" : qUnion([Q0]), "axis" : qUnion([Q1]), "revolveType" : RevolveType.FULL});
        }
        {
            var Q0;
            {var subQ0=sQuery(id+"F123.wireOp",EDGE,"E129");Q0=makeQuery(id+"F139.boolean.opBoolean","SPLIT",FACE,{"disambiguationData":[TD([makeQuery(id+"F129.opExtrude","CAP_FACE",FACE,{"disambiguationData":[OSD([sQuery(id+"F128.wireOp",EDGE,"E137.bottom"),sQuery(id+"F128.wireOp",EDGE,"E137.top"),sQuery(id+"F128.wireOp",EDGE,"E137.left"),sQuery(id+"F128.wireOp",EDGE,"E137.right")])],"isStart":true})])],"derivedFrom":makeQuery(id+"F139.opExtrude","CAP_FACE",FACE,{"disambiguationData":[OSD([subQ0])],"isStart":false})});}
            var Q1;
            Q1=makeQuery(id+"F139.boolean.opBoolean","INTERSECT",EDGE,{"derivedFrom":[makeQuery(id+"F138.opFillet","SPLIT",FACE,{"disambiguationData":[OD(0.0)],"derivedFrom":makeQuery(id+"F129.opExtrude","CAP_FACE",FACE,{"disambiguationData":[OSD([sQuery(id+"F128.wireOp",EDGE,"E137.bottom"),sQuery(id+"F128.wireOp",EDGE,"E137.top"),sQuery(id+"F128.wireOp",EDGE,"E137.left"),sQuery(id+"F128.wireOp",EDGE,"E137.right")])],"isStart":true})}),makeQuery(id+"F139.opExtrude","CAP_FACE",FACE,{"disambiguationData":[OSD([sQuery(id+"F123.wireOp",EDGE,"E129")])],"isStart":false})]});
            revolve(context, id + "F147", {"operationType" : NewBodyOperationType.ADD, "surfaceOperationType" : NewSurfaceOperationType.NEW, "entities" : qUnion([Q0]), "axis" : qUnion([Q1]), "revolveType" : RevolveType.FULL});
        }
        {
            var Q0;
            {var subQ0=sQuery(id+"F126.wireOp",EDGE,"E135");Q0=makeQuery(id+"F142.boolean.opBoolean","SPLIT",FACE,{"disambiguationData":[TD([makeQuery(id+"F129.opExtrude","CAP_FACE",FACE,{"disambiguationData":[OSD([sQuery(id+"F128.wireOp",EDGE,"E137.bottom"),sQuery(id+"F128.wireOp",EDGE,"E137.top"),sQuery(id+"F128.wireOp",EDGE,"E137.left"),sQuery(id+"F128.wireOp",EDGE,"E137.right")])],"isStart":true})])],"derivedFrom":makeQuery(id+"F142.opExtrude","CAP_FACE",FACE,{"disambiguationData":[OSD([subQ0])],"isStart":false})});}
            var Q1;
            Q1=makeQuery(id+"F142.boolean.opBoolean","INTERSECT",EDGE,{"derivedFrom":[makeQuery(id+"F138.opFillet","SPLIT",FACE,{"disambiguationData":[OD(2.0)],"derivedFrom":makeQuery(id+"F129.opExtrude","CAP_FACE",FACE,{"disambiguationData":[OSD([sQuery(id+"F128.wireOp",EDGE,"E137.bottom"),sQuery(id+"F128.wireOp",EDGE,"E137.top"),sQuery(id+"F128.wireOp",EDGE,"E137.left"),sQuery(id+"F128.wireOp",EDGE,"E137.right")])],"isStart":true})}),makeQuery(id+"F142.opExtrude","CAP_FACE",FACE,{"disambiguationData":[OSD([sQuery(id+"F126.wireOp",EDGE,"E135")])],"isStart":false})]});
            revolve(context, id + "F148", {"operationType" : NewBodyOperationType.ADD, "surfaceOperationType" : NewSurfaceOperationType.NEW, "entities" : qUnion([Q0]), "axis" : qUnion([Q1]), "revolveType" : RevolveType.FULL});
        }
        {
            var Q0;
            {var subQ0=sQuery(id+"F124.wireOp",EDGE,"E131");Q0=makeQuery(id+"F141.boolean.opBoolean","SPLIT",FACE,{"disambiguationData":[TD([makeQuery(id+"F129.opExtrude","CAP_FACE",FACE,{"disambiguationData":[OSD([sQuery(id+"F128.wireOp",EDGE,"E137.bottom"),sQuery(id+"F128.wireOp",EDGE,"E137.top"),sQuery(id+"F128.wireOp",EDGE,"E137.left"),sQuery(id+"F128.wireOp",EDGE,"E137.right")])],"isStart":true})])],"derivedFrom":makeQuery(id+"F141.opExtrude","CAP_FACE",FACE,{"disambiguationData":[OSD([subQ0])],"isStart":false})});}
            var Q1;
            Q1=makeQuery(id+"F141.boolean.opBoolean","INTERSECT",EDGE,{"derivedFrom":[makeQuery(id+"F138.opFillet","SPLIT",FACE,{"disambiguationData":[OD(1.0)],"derivedFrom":makeQuery(id+"F129.opExtrude","CAP_FACE",FACE,{"disambiguationData":[OSD([sQuery(id+"F128.wireOp",EDGE,"E137.bottom"),sQuery(id+"F128.wireOp",EDGE,"E137.top"),sQuery(id+"F128.wireOp",EDGE,"E137.left"),sQuery(id+"F128.wireOp",EDGE,"E137.right")])],"isStart":true})}),makeQuery(id+"F141.opExtrude","CAP_FACE",FACE,{"disambiguationData":[OSD([sQuery(id+"F124.wireOp",EDGE,"E131")])],"isStart":false})]});
            revolve(context, id + "F149", {"operationType" : NewBodyOperationType.ADD, "surfaceOperationType" : NewSurfaceOperationType.NEW, "entities" : qUnion([Q0]), "axis" : qUnion([Q1]), "revolveType" : RevolveType.FULL});
        }
        {
            var Q0;
            {var subQ0=sQuery(id+"F125.wireOp",EDGE,"E133");Q0=makeQuery(id+"F140.boolean.opBoolean","SPLIT",FACE,{"disambiguationData":[TD([makeQuery(id+"F129.opExtrude","CAP_FACE",FACE,{"disambiguationData":[OSD([sQuery(id+"F128.wireOp",EDGE,"E137.bottom"),sQuery(id+"F128.wireOp",EDGE,"E137.top"),sQuery(id+"F128.wireOp",EDGE,"E137.left"),sQuery(id+"F128.wireOp",EDGE,"E137.right")])],"isStart":true})])],"derivedFrom":makeQuery(id+"F140.opExtrude","CAP_FACE",FACE,{"disambiguationData":[OSD([subQ0])],"isStart":false})});}
            var Q1;
            Q1=makeQuery(id+"F140.boolean.opBoolean","INTERSECT",EDGE,{"derivedFrom":[makeQuery(id+"F138.opFillet","SPLIT",FACE,{"disambiguationData":[OD(3.0)],"derivedFrom":makeQuery(id+"F129.opExtrude","CAP_FACE",FACE,{"disambiguationData":[OSD([sQuery(id+"F128.wireOp",EDGE,"E137.bottom"),sQuery(id+"F128.wireOp",EDGE,"E137.top"),sQuery(id+"F128.wireOp",EDGE,"E137.left"),sQuery(id+"F128.wireOp",EDGE,"E137.right")])],"isStart":true})}),makeQuery(id+"F140.opExtrude","CAP_FACE",FACE,{"disambiguationData":[OSD([sQuery(id+"F125.wireOp",EDGE,"E133")])],"isStart":false})]});
            revolve(context, id + "F150", {"operationType" : NewBodyOperationType.ADD, "surfaceOperationType" : NewSurfaceOperationType.NEW, "entities" : qUnion([Q0]), "axis" : qUnion([Q1]), "revolveType" : RevolveType.FULL});
        }
    });
